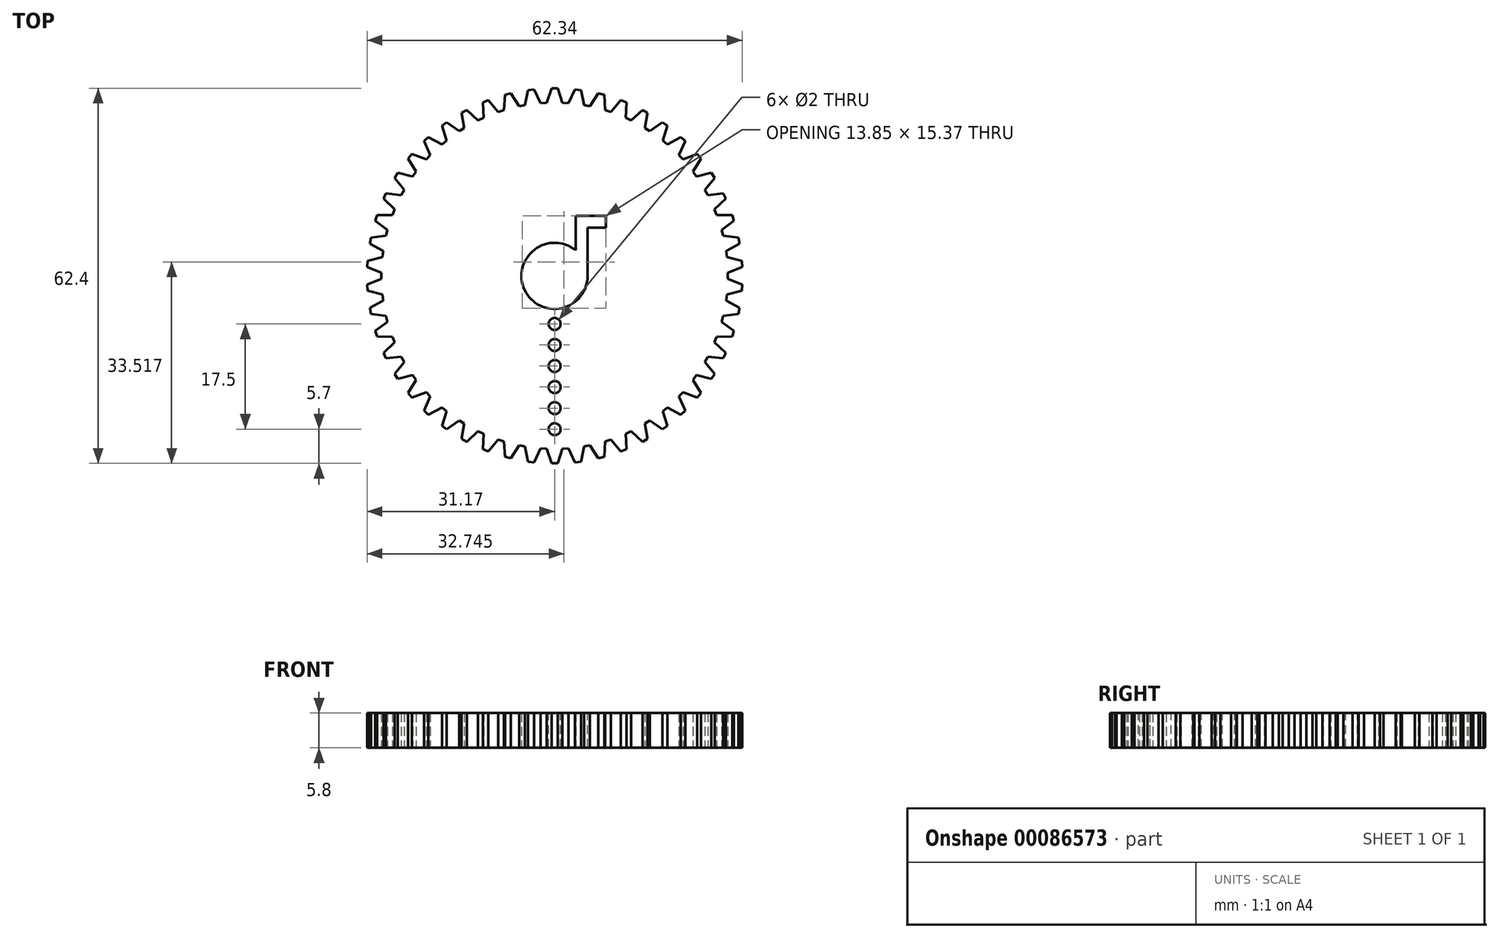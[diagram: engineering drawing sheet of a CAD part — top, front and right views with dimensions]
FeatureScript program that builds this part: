
annotation { "Feature Type Name" : "Feature", "Feature Type Description" : "" }
export const myFeature = defineFeature(function(context is Context, id is Id, definition is map)
    precondition{}
    {
        {
            var Q0;
            Q0=qCreatedBy(makeId("Top.planeOp"),FACE);
            var sketch = newSketch(context, id + "F0", { "sketchPlane" : qUnion([Q0])});
            skCircle(sketch, "E0", {"center": v(0, 0) * mm, "radius": 30 * mm, "construction": true});
            skCircle(sketch, "E1", {"center": v(0, 0) * mm, "radius": 31.2 * mm, "construction": true});
            skCircle(sketch, "E2", {"center": v(0, 0) * mm, "radius": 28.8 * mm, "construction": true});
            skPoint(sketch, "E3", {"position": v(0, 30) * mm});
            skPoint(sketch, "E4.1.0", {"position": v(-3.76, 29.76) * mm});
            skPoint(sketch, "E4.2.0", {"position": v(-7.46, 29.06) * mm});
            skPoint(sketch, "E4.3.0", {"position": v(-11.04, 27.9) * mm});
            skPoint(sketch, "E4.4.0", {"position": v(-14.45, 26.29) * mm});
            skPoint(sketch, "E4.5.0", {"position": v(-17.63, 24.27) * mm});
            skPoint(sketch, "E4.6.0", {"position": v(-20.54, 21.87) * mm});
            skPoint(sketch, "E4.7.0", {"position": v(-23.12, 19.12) * mm});
            skPoint(sketch, "E4.8.0", {"position": v(-25.33, 16.07) * mm});
            skPoint(sketch, "E4.9.0", {"position": v(-27.14, 12.77) * mm});
            skPoint(sketch, "E4.10.0", {"position": v(-28.53, 9.27) * mm});
            skPoint(sketch, "E4.11.0", {"position": v(-29.47, 5.62) * mm});
            skPoint(sketch, "E4.12.0", {"position": v(-29.94, 1.88) * mm});
            skPoint(sketch, "E4.13.0", {"position": v(-29.94, -1.88) * mm});
            skPoint(sketch, "E4.14.0", {"position": v(-29.47, -5.62) * mm});
            skPoint(sketch, "E4.15.0", {"position": v(-28.53, -9.27) * mm});
            skPoint(sketch, "E4.16.0", {"position": v(-27.14, -12.77) * mm});
            skPoint(sketch, "E4.17.0", {"position": v(-25.33, -16.07) * mm});
            skPoint(sketch, "E4.18.0", {"position": v(-23.12, -19.12) * mm});
            skPoint(sketch, "E4.19.0", {"position": v(-20.54, -21.87) * mm});
            skPoint(sketch, "E4.20.0", {"position": v(-17.63, -24.27) * mm});
            skPoint(sketch, "E4.21.0", {"position": v(-14.45, -26.29) * mm});
            skPoint(sketch, "E4.22.0", {"position": v(-11.04, -27.9) * mm});
            skPoint(sketch, "E4.23.0", {"position": v(-7.46, -29.06) * mm});
            skPoint(sketch, "E4.24.0", {"position": v(-3.76, -29.76) * mm});
            skPoint(sketch, "E4.25.0", {"position": v(0, -30) * mm});
            skPoint(sketch, "E4.26.0", {"position": v(3.76, -29.76) * mm});
            skPoint(sketch, "E4.27.0", {"position": v(7.46, -29.06) * mm});
            skPoint(sketch, "E4.28.0", {"position": v(11.04, -27.9) * mm});
            skPoint(sketch, "E4.29.0", {"position": v(14.45, -26.29) * mm});
            skPoint(sketch, "E4.30.0", {"position": v(17.63, -24.27) * mm});
            skPoint(sketch, "E4.31.0", {"position": v(20.54, -21.87) * mm});
            skPoint(sketch, "E4.32.0", {"position": v(23.12, -19.12) * mm});
            skPoint(sketch, "E4.33.0", {"position": v(25.33, -16.07) * mm});
            skPoint(sketch, "E4.34.0", {"position": v(27.14, -12.77) * mm});
            skPoint(sketch, "E4.35.0", {"position": v(28.53, -9.27) * mm});
            skPoint(sketch, "E4.36.0", {"position": v(29.47, -5.62) * mm});
            skPoint(sketch, "E4.37.0", {"position": v(29.94, -1.88) * mm});
            skPoint(sketch, "E4.38.0", {"position": v(29.94, 1.88) * mm});
            skPoint(sketch, "E4.39.0", {"position": v(29.47, 5.62) * mm});
            skPoint(sketch, "E4.40.0", {"position": v(28.53, 9.27) * mm});
            skPoint(sketch, "E4.41.0", {"position": v(27.14, 12.77) * mm});
            skPoint(sketch, "E4.42.0", {"position": v(25.33, 16.07) * mm});
            skPoint(sketch, "E4.43.0", {"position": v(23.12, 19.12) * mm});
            skPoint(sketch, "E4.44.0", {"position": v(20.54, 21.87) * mm});
            skPoint(sketch, "E4.45.0", {"position": v(17.63, 24.27) * mm});
            skPoint(sketch, "E4.46.0", {"position": v(14.45, 26.29) * mm});
            skPoint(sketch, "E4.47.0", {"position": v(11.04, 27.9) * mm});
            skPoint(sketch, "E4.48.0", {"position": v(7.46, 29.06) * mm});
            skPoint(sketch, "E4.49.0", {"position": v(3.76, 29.76) * mm});
            skLineSegment(sketch, "E5", {"start": v(0, 30) * mm, "end": v(3.76, 29.76) * mm, "construction": true});
            skLineSegment(sketch, "E6", {"start": v(1.88, 29.88) * mm, "end": v(0, 0) * mm, "construction": true});
            skLineSegment(sketch, "E7", {"start": v(0, 31.2) * mm, "end": v(0.5, 31.2) * mm});
            skLineSegment(sketch, "E8", {"start": v(1.8, 28.74) * mm, "end": v(1.3, 28.77) * mm});
            skLineSegment(sketch, "E9", {"start": v(0.5, 31.2) * mm, "end": v(1.3, 28.77) * mm});
            skLineSegment(sketch, "E10", {"start": v(3.76, 29.76) * mm, "end": v(0, 0) * mm, "construction": true});
            skLineSegment(sketch, "E11", {"start": v(1.8, 28.74) * mm, "end": v(2.3, 28.71) * mm});
            skLineSegment(sketch, "E12", {"start": v(3.76, 29.76) * mm, "end": v(3.91, 30.95) * mm, "construction": true});
            skLineSegment(sketch, "E13", {"start": v(3.91, 30.95) * mm, "end": v(3.41, 31.02) * mm});
            skLineSegment(sketch, "E14", {"start": v(2.3, 28.71) * mm, "end": v(3.41, 31.02) * mm});
            skLineSegment(sketch, "E15.1.1", {"start": v(-3.76, 29.76) * mm, "end": v(0, 30) * mm, "construction": true});
            skLineSegment(sketch, "E15.1.2", {"start": v(-3.41, 31.02) * mm, "end": v(-2.3, 28.71) * mm});
            skLineSegment(sketch, "E15.1.3", {"start": v(0, 30) * mm, "end": v(0, 31.2) * mm, "construction": true});
            skLineSegment(sketch, "E15.1.4", {"start": v(-1.3, 28.77) * mm, "end": v(-0.5, 31.2) * mm});
            skLineSegment(sketch, "E15.1.6", {"start": v(-3.91, 30.95) * mm, "end": v(-3.41, 31.02) * mm});
            skLineSegment(sketch, "E15.1.7", {"start": v(-1.8, 28.74) * mm, "end": v(-2.3, 28.71) * mm});
            skLineSegment(sketch, "E15.1.8", {"start": v(-1.8, 28.74) * mm, "end": v(-1.3, 28.77) * mm});
            skLineSegment(sketch, "E15.1.9", {"start": v(0, 31.2) * mm, "end": v(-0.5, 31.2) * mm});
            skLineSegment(sketch, "E15.2.1", {"start": v(-7.46, 29.06) * mm, "end": v(-3.76, 29.76) * mm, "construction": true});
            skLineSegment(sketch, "E15.2.2", {"start": v(-7.27, 30.34) * mm, "end": v(-5.89, 28.2) * mm});
            skLineSegment(sketch, "E15.2.3", {"start": v(-3.76, 29.76) * mm, "end": v(-3.91, 30.95) * mm, "construction": true});
            skLineSegment(sketch, "E15.2.4", {"start": v(-4.9, 28.38) * mm, "end": v(-4.4, 30.9) * mm});
            skLineSegment(sketch, "E15.2.6", {"start": v(-7.76, 30.22) * mm, "end": v(-7.27, 30.34) * mm});
            skLineSegment(sketch, "E15.2.7", {"start": v(-5.4, 28.29) * mm, "end": v(-5.89, 28.2) * mm});
            skLineSegment(sketch, "E15.2.8", {"start": v(-5.4, 28.29) * mm, "end": v(-4.9, 28.38) * mm});
            skLineSegment(sketch, "E15.2.9", {"start": v(-3.91, 30.95) * mm, "end": v(-4.4, 30.9) * mm});
            skLineSegment(sketch, "E15.3.1", {"start": v(-11.04, 27.9) * mm, "end": v(-7.46, 29.06) * mm, "construction": true});
            skLineSegment(sketch, "E15.3.2", {"start": v(-11.02, 29.2) * mm, "end": v(-9.38, 27.24) * mm});
            skLineSegment(sketch, "E15.3.3", {"start": v(-7.46, 29.06) * mm, "end": v(-7.76, 30.22) * mm, "construction": true});
            skLineSegment(sketch, "E15.3.4", {"start": v(-8.42, 27.54) * mm, "end": v(-8.24, 30.1) * mm});
            skLineSegment(sketch, "E15.3.6", {"start": v(-11.49, 29) * mm, "end": v(-11.02, 29.2) * mm});
            skLineSegment(sketch, "E15.3.7", {"start": v(-8.9, 27.4) * mm, "end": v(-9.38, 27.24) * mm});
            skLineSegment(sketch, "E15.3.8", {"start": v(-8.9, 27.4) * mm, "end": v(-8.42, 27.54) * mm});
            skLineSegment(sketch, "E15.3.9", {"start": v(-7.76, 30.22) * mm, "end": v(-8.24, 30.1) * mm});
            skLineSegment(sketch, "E15.4.1", {"start": v(-14.45, 26.29) * mm, "end": v(-11.04, 27.9) * mm, "construction": true});
            skLineSegment(sketch, "E15.4.2", {"start": v(-14.6, 27.58) * mm, "end": v(-12.71, 25.85) * mm});
            skLineSegment(sketch, "E15.4.3", {"start": v(-11.04, 27.9) * mm, "end": v(-11.49, 29) * mm, "construction": true});
            skLineSegment(sketch, "E15.4.4", {"start": v(-11.81, 26.27) * mm, "end": v(-11.95, 28.82) * mm});
            skLineSegment(sketch, "E15.4.6", {"start": v(-15.03, 27.34) * mm, "end": v(-14.6, 27.58) * mm});
            skLineSegment(sketch, "E15.4.7", {"start": v(-12.26, 26.06) * mm, "end": v(-12.71, 25.85) * mm});
            skLineSegment(sketch, "E15.4.8", {"start": v(-12.26, 26.06) * mm, "end": v(-11.81, 26.27) * mm});
            skLineSegment(sketch, "E15.4.9", {"start": v(-11.49, 29) * mm, "end": v(-11.95, 28.82) * mm});
            skLineSegment(sketch, "E15.5.1", {"start": v(-17.63, 24.27) * mm, "end": v(-14.45, 26.29) * mm, "construction": true});
            skLineSegment(sketch, "E15.5.2", {"start": v(-17.93, 25.54) * mm, "end": v(-15.85, 24.05) * mm});
            skLineSegment(sketch, "E15.5.3", {"start": v(-14.45, 26.29) * mm, "end": v(-15.03, 27.34) * mm, "construction": true});
            skLineSegment(sketch, "E15.5.4", {"start": v(-15, 24.58) * mm, "end": v(-15.47, 27.1) * mm});
            skLineSegment(sketch, "E15.5.6", {"start": v(-18.34, 25.24) * mm, "end": v(-17.93, 25.54) * mm});
            skLineSegment(sketch, "E15.5.7", {"start": v(-15.43, 24.32) * mm, "end": v(-15.85, 24.05) * mm});
            skLineSegment(sketch, "E15.5.8", {"start": v(-15.43, 24.32) * mm, "end": v(-15, 24.58) * mm});
            skLineSegment(sketch, "E15.5.9", {"start": v(-15.03, 27.34) * mm, "end": v(-15.47, 27.1) * mm});
            skLineSegment(sketch, "E15.6.1", {"start": v(-20.54, 21.87) * mm, "end": v(-17.63, 24.27) * mm, "construction": true});
            skLineSegment(sketch, "E15.6.2", {"start": v(-21, 23.09) * mm, "end": v(-18.74, 21.87) * mm});
            skLineSegment(sketch, "E15.6.3", {"start": v(-17.63, 24.27) * mm, "end": v(-18.34, 25.24) * mm, "construction": true});
            skLineSegment(sketch, "E15.6.4", {"start": v(-17.97, 22.5) * mm, "end": v(-18.74, 24.95) * mm});
            skLineSegment(sketch, "E15.6.6", {"start": v(-21.36, 22.74) * mm, "end": v(-21, 23.09) * mm});
            skLineSegment(sketch, "E15.6.7", {"start": v(-18.36, 22.2) * mm, "end": v(-18.74, 21.87) * mm});
            skLineSegment(sketch, "E15.6.8", {"start": v(-18.36, 22.2) * mm, "end": v(-17.97, 22.5) * mm});
            skLineSegment(sketch, "E15.6.9", {"start": v(-18.34, 25.24) * mm, "end": v(-18.74, 24.95) * mm});
            skLineSegment(sketch, "E15.7.1", {"start": v(-23.12, 19.12) * mm, "end": v(-20.54, 21.87) * mm, "construction": true});
            skLineSegment(sketch, "E15.7.2", {"start": v(-23.72, 20.27) * mm, "end": v(-21.34, 19.35) * mm});
            skLineSegment(sketch, "E15.7.3", {"start": v(-20.54, 21.87) * mm, "end": v(-21.36, 22.74) * mm, "construction": true});
            skLineSegment(sketch, "E15.7.4", {"start": v(-20.65, 20.08) * mm, "end": v(-21.72, 22.4) * mm});
            skLineSegment(sketch, "E15.7.6", {"start": v(-24.04, 19.89) * mm, "end": v(-23.72, 20.27) * mm});
            skLineSegment(sketch, "E15.7.7", {"start": v(-21, 19.71) * mm, "end": v(-21.34, 19.35) * mm});
            skLineSegment(sketch, "E15.7.8", {"start": v(-21, 19.71) * mm, "end": v(-20.65, 20.08) * mm});
            skLineSegment(sketch, "E15.7.9", {"start": v(-21.36, 22.74) * mm, "end": v(-21.72, 22.4) * mm});
            skLineSegment(sketch, "E15.8.1", {"start": v(-25.33, 16.07) * mm, "end": v(-23.12, 19.12) * mm, "construction": true});
            skLineSegment(sketch, "E15.8.2", {"start": v(-26.08, 17.14) * mm, "end": v(-23.6, 16.52) * mm});
            skLineSegment(sketch, "E15.8.3", {"start": v(-23.12, 19.12) * mm, "end": v(-24.04, 19.89) * mm, "construction": true});
            skLineSegment(sketch, "E15.8.4", {"start": v(-23, 17.33) * mm, "end": v(-24.36, 19.5) * mm});
            skLineSegment(sketch, "E15.8.6", {"start": v(-26.34, 16.72) * mm, "end": v(-26.08, 17.14) * mm});
            skLineSegment(sketch, "E15.8.7", {"start": v(-23.3, 16.93) * mm, "end": v(-23.6, 16.52) * mm});
            skLineSegment(sketch, "E15.8.8", {"start": v(-23.3, 16.93) * mm, "end": v(-23, 17.33) * mm});
            skLineSegment(sketch, "E15.8.9", {"start": v(-24.04, 19.89) * mm, "end": v(-24.36, 19.5) * mm});
            skLineSegment(sketch, "E15.9.1", {"start": v(-27.14, 12.77) * mm, "end": v(-25.33, 16.07) * mm, "construction": true});
            skLineSegment(sketch, "E15.9.2", {"start": v(-28.02, 13.74) * mm, "end": v(-25.48, 13.44) * mm});
            skLineSegment(sketch, "E15.9.3", {"start": v(-25.33, 16.07) * mm, "end": v(-26.34, 16.72) * mm, "construction": true});
            skLineSegment(sketch, "E15.9.4", {"start": v(-25, 14.31) * mm, "end": v(-26.61, 16.3) * mm});
            skLineSegment(sketch, "E15.9.6", {"start": v(-28.23, 13.28) * mm, "end": v(-28.02, 13.74) * mm});
            skLineSegment(sketch, "E15.9.7", {"start": v(-25.24, 13.87) * mm, "end": v(-25.48, 13.44) * mm});
            skLineSegment(sketch, "E15.9.8", {"start": v(-25.24, 13.87) * mm, "end": v(-25, 14.31) * mm});
            skLineSegment(sketch, "E15.9.9", {"start": v(-26.34, 16.72) * mm, "end": v(-26.61, 16.3) * mm});
            skLineSegment(sketch, "E15.10.1", {"start": v(-28.53, 9.27) * mm, "end": v(-27.14, 12.77) * mm, "construction": true});
            skLineSegment(sketch, "E15.10.2", {"start": v(-29.52, 10.12) * mm, "end": v(-26.96, 10.14) * mm});
            skLineSegment(sketch, "E15.10.3", {"start": v(-27.14, 12.77) * mm, "end": v(-28.23, 13.28) * mm, "construction": true});
            skLineSegment(sketch, "E15.10.4", {"start": v(-26.6, 11.07) * mm, "end": v(-28.44, 12.83) * mm});
            skLineSegment(sketch, "E15.10.6", {"start": v(-29.67, 9.64) * mm, "end": v(-29.52, 10.12) * mm});
            skLineSegment(sketch, "E15.10.7", {"start": v(-26.78, 10.6) * mm, "end": v(-26.96, 10.14) * mm});
            skLineSegment(sketch, "E15.10.8", {"start": v(-26.78, 10.6) * mm, "end": v(-26.6, 11.07) * mm});
            skLineSegment(sketch, "E15.10.9", {"start": v(-28.23, 13.28) * mm, "end": v(-28.44, 12.83) * mm});
            skLineSegment(sketch, "E15.11.1", {"start": v(-29.47, 5.62) * mm, "end": v(-28.53, 9.27) * mm, "construction": true});
            skLineSegment(sketch, "E15.11.2", {"start": v(-30.55, 6.34) * mm, "end": v(-28.02, 6.68) * mm});
            skLineSegment(sketch, "E15.11.3", {"start": v(-28.53, 9.27) * mm, "end": v(-29.67, 9.64) * mm, "construction": true});
            skLineSegment(sketch, "E15.11.4", {"start": v(-27.77, 7.65) * mm, "end": v(-29.83, 9.17) * mm});
            skLineSegment(sketch, "E15.11.6", {"start": v(-30.65, 5.85) * mm, "end": v(-30.55, 6.34) * mm});
            skLineSegment(sketch, "E15.11.7", {"start": v(-27.9, 7.16) * mm, "end": v(-28.02, 6.68) * mm});
            skLineSegment(sketch, "E15.11.8", {"start": v(-27.9, 7.16) * mm, "end": v(-27.77, 7.65) * mm});
            skLineSegment(sketch, "E15.11.9", {"start": v(-29.67, 9.64) * mm, "end": v(-29.83, 9.17) * mm});
            skLineSegment(sketch, "E15.12.1", {"start": v(-29.94, 1.88) * mm, "end": v(-29.47, 5.62) * mm, "construction": true});
            skLineSegment(sketch, "E15.12.2", {"start": v(-31.1, 2.46) * mm, "end": v(-28.64, 3.11) * mm});
            skLineSegment(sketch, "E15.12.3", {"start": v(-29.47, 5.62) * mm, "end": v(-30.65, 5.85) * mm, "construction": true});
            skLineSegment(sketch, "E15.12.4", {"start": v(-28.51, 4.1) * mm, "end": v(-30.74, 5.36) * mm});
            skLineSegment(sketch, "E15.12.6", {"start": v(-31.14, 1.96) * mm, "end": v(-31.1, 2.46) * mm});
            skLineSegment(sketch, "E15.12.7", {"start": v(-28.57, 3.6) * mm, "end": v(-28.64, 3.11) * mm});
            skLineSegment(sketch, "E15.12.8", {"start": v(-28.57, 3.6) * mm, "end": v(-28.51, 4.1) * mm});
            skLineSegment(sketch, "E15.12.9", {"start": v(-30.65, 5.85) * mm, "end": v(-30.74, 5.36) * mm});
            skLineSegment(sketch, "E15.13.1", {"start": v(-29.94, -1.88) * mm, "end": v(-29.94, 1.88) * mm, "construction": true});
            skLineSegment(sketch, "E15.13.2", {"start": v(-31.17, -1.46) * mm, "end": v(-28.8, -0.5) * mm});
            skLineSegment(sketch, "E15.13.3", {"start": v(-29.94, 1.88) * mm, "end": v(-31.14, 1.96) * mm, "construction": true});
            skLineSegment(sketch, "E15.13.4", {"start": v(-28.8, 0.5) * mm, "end": v(-31.17, 1.46) * mm});
            skLineSegment(sketch, "E15.13.6", {"start": v(-31.14, -1.96) * mm, "end": v(-31.17, -1.46) * mm});
            skLineSegment(sketch, "E15.13.7", {"start": v(-28.8, 0) * mm, "end": v(-28.8, -0.5) * mm});
            skLineSegment(sketch, "E15.13.8", {"start": v(-28.8, 0) * mm, "end": v(-28.8, 0.5) * mm});
            skLineSegment(sketch, "E15.13.9", {"start": v(-31.14, 1.96) * mm, "end": v(-31.17, 1.46) * mm});
            skLineSegment(sketch, "E15.14.1", {"start": v(-29.47, -5.62) * mm, "end": v(-29.94, -1.88) * mm, "construction": true});
            skLineSegment(sketch, "E15.14.2", {"start": v(-30.74, -5.36) * mm, "end": v(-28.51, -4.1) * mm});
            skLineSegment(sketch, "E15.14.3", {"start": v(-29.94, -1.88) * mm, "end": v(-31.14, -1.96) * mm, "construction": true});
            skLineSegment(sketch, "E15.14.4", {"start": v(-28.64, -3.11) * mm, "end": v(-31.1, -2.46) * mm});
            skLineSegment(sketch, "E15.14.6", {"start": v(-30.65, -5.85) * mm, "end": v(-30.74, -5.36) * mm});
            skLineSegment(sketch, "E15.14.7", {"start": v(-28.57, -3.6) * mm, "end": v(-28.51, -4.1) * mm});
            skLineSegment(sketch, "E15.14.8", {"start": v(-28.57, -3.6) * mm, "end": v(-28.64, -3.11) * mm});
            skLineSegment(sketch, "E15.14.9", {"start": v(-31.14, -1.96) * mm, "end": v(-31.1, -2.46) * mm});
            skLineSegment(sketch, "E15.15.1", {"start": v(-28.53, -9.27) * mm, "end": v(-29.47, -5.62) * mm, "construction": true});
            skLineSegment(sketch, "E15.15.2", {"start": v(-29.83, -9.17) * mm, "end": v(-27.77, -7.65) * mm});
            skLineSegment(sketch, "E15.15.3", {"start": v(-29.47, -5.62) * mm, "end": v(-30.65, -5.85) * mm, "construction": true});
            skLineSegment(sketch, "E15.15.4", {"start": v(-28.02, -6.68) * mm, "end": v(-30.55, -6.34) * mm});
            skLineSegment(sketch, "E15.15.6", {"start": v(-29.67, -9.64) * mm, "end": v(-29.83, -9.17) * mm});
            skLineSegment(sketch, "E15.15.7", {"start": v(-27.9, -7.16) * mm, "end": v(-27.77, -7.65) * mm});
            skLineSegment(sketch, "E15.15.8", {"start": v(-27.9, -7.16) * mm, "end": v(-28.02, -6.68) * mm});
            skLineSegment(sketch, "E15.15.9", {"start": v(-30.65, -5.85) * mm, "end": v(-30.55, -6.34) * mm});
            skLineSegment(sketch, "E15.16.1", {"start": v(-27.14, -12.77) * mm, "end": v(-28.53, -9.27) * mm, "construction": true});
            skLineSegment(sketch, "E15.16.2", {"start": v(-28.44, -12.83) * mm, "end": v(-26.6, -11.07) * mm});
            skLineSegment(sketch, "E15.16.3", {"start": v(-28.53, -9.27) * mm, "end": v(-29.67, -9.64) * mm, "construction": true});
            skLineSegment(sketch, "E15.16.4", {"start": v(-26.96, -10.14) * mm, "end": v(-29.52, -10.12) * mm});
            skLineSegment(sketch, "E15.16.6", {"start": v(-28.23, -13.28) * mm, "end": v(-28.44, -12.83) * mm});
            skLineSegment(sketch, "E15.16.7", {"start": v(-26.78, -10.6) * mm, "end": v(-26.6, -11.07) * mm});
            skLineSegment(sketch, "E15.16.8", {"start": v(-26.78, -10.6) * mm, "end": v(-26.96, -10.14) * mm});
            skLineSegment(sketch, "E15.16.9", {"start": v(-29.67, -9.64) * mm, "end": v(-29.52, -10.12) * mm});
            skLineSegment(sketch, "E15.17.1", {"start": v(-25.33, -16.07) * mm, "end": v(-27.14, -12.77) * mm, "construction": true});
            skLineSegment(sketch, "E15.17.2", {"start": v(-26.61, -16.3) * mm, "end": v(-25, -14.31) * mm});
            skLineSegment(sketch, "E15.17.3", {"start": v(-27.14, -12.77) * mm, "end": v(-28.23, -13.28) * mm, "construction": true});
            skLineSegment(sketch, "E15.17.4", {"start": v(-25.48, -13.44) * mm, "end": v(-28.02, -13.74) * mm});
            skLineSegment(sketch, "E15.17.6", {"start": v(-26.34, -16.72) * mm, "end": v(-26.61, -16.3) * mm});
            skLineSegment(sketch, "E15.17.7", {"start": v(-25.24, -13.87) * mm, "end": v(-25, -14.31) * mm});
            skLineSegment(sketch, "E15.17.8", {"start": v(-25.24, -13.87) * mm, "end": v(-25.48, -13.44) * mm});
            skLineSegment(sketch, "E15.17.9", {"start": v(-28.23, -13.28) * mm, "end": v(-28.02, -13.74) * mm});
            skLineSegment(sketch, "E15.18.1", {"start": v(-23.12, -19.12) * mm, "end": v(-25.33, -16.07) * mm, "construction": true});
            skLineSegment(sketch, "E15.18.2", {"start": v(-24.36, -19.5) * mm, "end": v(-23, -17.33) * mm});
            skLineSegment(sketch, "E15.18.3", {"start": v(-25.33, -16.07) * mm, "end": v(-26.34, -16.72) * mm, "construction": true});
            skLineSegment(sketch, "E15.18.4", {"start": v(-23.6, -16.52) * mm, "end": v(-26.08, -17.14) * mm});
            skLineSegment(sketch, "E15.18.6", {"start": v(-24.04, -19.89) * mm, "end": v(-24.36, -19.5) * mm});
            skLineSegment(sketch, "E15.18.7", {"start": v(-23.3, -16.93) * mm, "end": v(-23, -17.33) * mm});
            skLineSegment(sketch, "E15.18.8", {"start": v(-23.3, -16.93) * mm, "end": v(-23.6, -16.52) * mm});
            skLineSegment(sketch, "E15.18.9", {"start": v(-26.34, -16.72) * mm, "end": v(-26.08, -17.14) * mm});
            skLineSegment(sketch, "E15.19.1", {"start": v(-20.54, -21.87) * mm, "end": v(-23.12, -19.12) * mm, "construction": true});
            skLineSegment(sketch, "E15.19.2", {"start": v(-21.72, -22.4) * mm, "end": v(-20.65, -20.08) * mm});
            skLineSegment(sketch, "E15.19.3", {"start": v(-23.12, -19.12) * mm, "end": v(-24.04, -19.89) * mm, "construction": true});
            skLineSegment(sketch, "E15.19.4", {"start": v(-21.34, -19.35) * mm, "end": v(-23.72, -20.27) * mm});
            skLineSegment(sketch, "E15.19.6", {"start": v(-21.36, -22.74) * mm, "end": v(-21.72, -22.4) * mm});
            skLineSegment(sketch, "E15.19.7", {"start": v(-21, -19.71) * mm, "end": v(-20.65, -20.08) * mm});
            skLineSegment(sketch, "E15.19.8", {"start": v(-21, -19.71) * mm, "end": v(-21.34, -19.35) * mm});
            skLineSegment(sketch, "E15.19.9", {"start": v(-24.04, -19.89) * mm, "end": v(-23.72, -20.27) * mm});
            skLineSegment(sketch, "E15.20.1", {"start": v(-17.63, -24.27) * mm, "end": v(-20.54, -21.87) * mm, "construction": true});
            skLineSegment(sketch, "E15.20.2", {"start": v(-18.74, -24.95) * mm, "end": v(-17.97, -22.5) * mm});
            skLineSegment(sketch, "E15.20.3", {"start": v(-20.54, -21.87) * mm, "end": v(-21.36, -22.74) * mm, "construction": true});
            skLineSegment(sketch, "E15.20.4", {"start": v(-18.74, -21.87) * mm, "end": v(-21, -23.09) * mm});
            skLineSegment(sketch, "E15.20.6", {"start": v(-18.34, -25.24) * mm, "end": v(-18.74, -24.95) * mm});
            skLineSegment(sketch, "E15.20.7", {"start": v(-18.36, -22.2) * mm, "end": v(-17.97, -22.5) * mm});
            skLineSegment(sketch, "E15.20.8", {"start": v(-18.36, -22.2) * mm, "end": v(-18.74, -21.87) * mm});
            skLineSegment(sketch, "E15.20.9", {"start": v(-21.36, -22.74) * mm, "end": v(-21, -23.09) * mm});
            skLineSegment(sketch, "E15.21.1", {"start": v(-14.45, -26.29) * mm, "end": v(-17.63, -24.27) * mm, "construction": true});
            skLineSegment(sketch, "E15.21.2", {"start": v(-15.47, -27.1) * mm, "end": v(-15, -24.58) * mm});
            skLineSegment(sketch, "E15.21.3", {"start": v(-17.63, -24.27) * mm, "end": v(-18.34, -25.24) * mm, "construction": true});
            skLineSegment(sketch, "E15.21.4", {"start": v(-15.85, -24.05) * mm, "end": v(-17.93, -25.54) * mm});
            skLineSegment(sketch, "E15.21.6", {"start": v(-15.03, -27.34) * mm, "end": v(-15.47, -27.1) * mm});
            skLineSegment(sketch, "E15.21.7", {"start": v(-15.43, -24.32) * mm, "end": v(-15, -24.58) * mm});
            skLineSegment(sketch, "E15.21.8", {"start": v(-15.43, -24.32) * mm, "end": v(-15.85, -24.05) * mm});
            skLineSegment(sketch, "E15.21.9", {"start": v(-18.34, -25.24) * mm, "end": v(-17.93, -25.54) * mm});
            skLineSegment(sketch, "E15.22.1", {"start": v(-11.04, -27.9) * mm, "end": v(-14.45, -26.29) * mm, "construction": true});
            skLineSegment(sketch, "E15.22.2", {"start": v(-11.95, -28.82) * mm, "end": v(-11.81, -26.27) * mm});
            skLineSegment(sketch, "E15.22.3", {"start": v(-14.45, -26.29) * mm, "end": v(-15.03, -27.34) * mm, "construction": true});
            skLineSegment(sketch, "E15.22.4", {"start": v(-12.71, -25.85) * mm, "end": v(-14.6, -27.58) * mm});
            skLineSegment(sketch, "E15.22.6", {"start": v(-11.49, -29) * mm, "end": v(-11.95, -28.82) * mm});
            skLineSegment(sketch, "E15.22.7", {"start": v(-12.26, -26.06) * mm, "end": v(-11.81, -26.27) * mm});
            skLineSegment(sketch, "E15.22.8", {"start": v(-12.26, -26.06) * mm, "end": v(-12.71, -25.85) * mm});
            skLineSegment(sketch, "E15.22.9", {"start": v(-15.03, -27.34) * mm, "end": v(-14.6, -27.58) * mm});
            skLineSegment(sketch, "E15.23.1", {"start": v(-7.46, -29.06) * mm, "end": v(-11.04, -27.9) * mm, "construction": true});
            skLineSegment(sketch, "E15.23.2", {"start": v(-8.24, -30.1) * mm, "end": v(-8.42, -27.54) * mm});
            skLineSegment(sketch, "E15.23.3", {"start": v(-11.04, -27.9) * mm, "end": v(-11.49, -29) * mm, "construction": true});
            skLineSegment(sketch, "E15.23.4", {"start": v(-9.38, -27.24) * mm, "end": v(-11.02, -29.2) * mm});
            skLineSegment(sketch, "E15.23.6", {"start": v(-7.76, -30.22) * mm, "end": v(-8.24, -30.1) * mm});
            skLineSegment(sketch, "E15.23.7", {"start": v(-8.9, -27.4) * mm, "end": v(-8.42, -27.54) * mm});
            skLineSegment(sketch, "E15.23.8", {"start": v(-8.9, -27.4) * mm, "end": v(-9.38, -27.24) * mm});
            skLineSegment(sketch, "E15.23.9", {"start": v(-11.49, -29) * mm, "end": v(-11.02, -29.2) * mm});
            skLineSegment(sketch, "E15.24.1", {"start": v(-3.76, -29.76) * mm, "end": v(-7.46, -29.06) * mm, "construction": true});
            skLineSegment(sketch, "E15.24.2", {"start": v(-4.4, -30.9) * mm, "end": v(-4.9, -28.38) * mm});
            skLineSegment(sketch, "E15.24.3", {"start": v(-7.46, -29.06) * mm, "end": v(-7.76, -30.22) * mm, "construction": true});
            skLineSegment(sketch, "E15.24.4", {"start": v(-5.89, -28.2) * mm, "end": v(-7.27, -30.34) * mm});
            skLineSegment(sketch, "E15.24.6", {"start": v(-3.91, -30.95) * mm, "end": v(-4.4, -30.9) * mm});
            skLineSegment(sketch, "E15.24.7", {"start": v(-5.4, -28.29) * mm, "end": v(-4.9, -28.38) * mm});
            skLineSegment(sketch, "E15.24.8", {"start": v(-5.4, -28.29) * mm, "end": v(-5.89, -28.2) * mm});
            skLineSegment(sketch, "E15.24.9", {"start": v(-7.76, -30.22) * mm, "end": v(-7.27, -30.34) * mm});
            skLineSegment(sketch, "E15.25.1", {"start": v(0, -30) * mm, "end": v(-3.76, -29.76) * mm, "construction": true});
            skLineSegment(sketch, "E15.25.2", {"start": v(-0.5, -31.2) * mm, "end": v(-1.3, -28.77) * mm});
            skLineSegment(sketch, "E15.25.3", {"start": v(-3.76, -29.76) * mm, "end": v(-3.91, -30.95) * mm, "construction": true});
            skLineSegment(sketch, "E15.25.4", {"start": v(-2.3, -28.71) * mm, "end": v(-3.41, -31.02) * mm});
            skLineSegment(sketch, "E15.25.6", {"start": v(0, -31.2) * mm, "end": v(-0.5, -31.2) * mm});
            skLineSegment(sketch, "E15.25.7", {"start": v(-1.8, -28.74) * mm, "end": v(-1.3, -28.77) * mm});
            skLineSegment(sketch, "E15.25.8", {"start": v(-1.8, -28.74) * mm, "end": v(-2.3, -28.71) * mm});
            skLineSegment(sketch, "E15.25.9", {"start": v(-3.91, -30.95) * mm, "end": v(-3.41, -31.02) * mm});
            skLineSegment(sketch, "E15.26.1", {"start": v(3.76, -29.76) * mm, "end": v(0, -30) * mm, "construction": true});
            skLineSegment(sketch, "E15.26.2", {"start": v(3.41, -31.02) * mm, "end": v(2.3, -28.71) * mm});
            skLineSegment(sketch, "E15.26.3", {"start": v(0, -30) * mm, "end": v(0, -31.2) * mm, "construction": true});
            skLineSegment(sketch, "E15.26.4", {"start": v(1.3, -28.77) * mm, "end": v(0.5, -31.2) * mm});
            skLineSegment(sketch, "E15.26.6", {"start": v(3.91, -30.95) * mm, "end": v(3.41, -31.02) * mm});
            skLineSegment(sketch, "E15.26.7", {"start": v(1.8, -28.74) * mm, "end": v(2.3, -28.71) * mm});
            skLineSegment(sketch, "E15.26.8", {"start": v(1.8, -28.74) * mm, "end": v(1.3, -28.77) * mm});
            skLineSegment(sketch, "E15.26.9", {"start": v(0, -31.2) * mm, "end": v(0.5, -31.2) * mm});
            skLineSegment(sketch, "E15.27.1", {"start": v(7.46, -29.06) * mm, "end": v(3.76, -29.76) * mm, "construction": true});
            skLineSegment(sketch, "E15.27.2", {"start": v(7.27, -30.34) * mm, "end": v(5.89, -28.2) * mm});
            skLineSegment(sketch, "E15.27.3", {"start": v(3.76, -29.76) * mm, "end": v(3.91, -30.95) * mm, "construction": true});
            skLineSegment(sketch, "E15.27.4", {"start": v(4.9, -28.38) * mm, "end": v(4.4, -30.9) * mm});
            skLineSegment(sketch, "E15.27.6", {"start": v(7.76, -30.22) * mm, "end": v(7.27, -30.34) * mm});
            skLineSegment(sketch, "E15.27.7", {"start": v(5.4, -28.29) * mm, "end": v(5.89, -28.2) * mm});
            skLineSegment(sketch, "E15.27.8", {"start": v(5.4, -28.29) * mm, "end": v(4.9, -28.38) * mm});
            skLineSegment(sketch, "E15.27.9", {"start": v(3.91, -30.95) * mm, "end": v(4.4, -30.9) * mm});
            skLineSegment(sketch, "E15.28.1", {"start": v(11.04, -27.9) * mm, "end": v(7.46, -29.06) * mm, "construction": true});
            skLineSegment(sketch, "E15.28.2", {"start": v(11.02, -29.2) * mm, "end": v(9.38, -27.24) * mm});
            skLineSegment(sketch, "E15.28.3", {"start": v(7.46, -29.06) * mm, "end": v(7.76, -30.22) * mm, "construction": true});
            skLineSegment(sketch, "E15.28.4", {"start": v(8.42, -27.54) * mm, "end": v(8.24, -30.1) * mm});
            skLineSegment(sketch, "E15.28.6", {"start": v(11.49, -29) * mm, "end": v(11.02, -29.2) * mm});
            skLineSegment(sketch, "E15.28.7", {"start": v(8.9, -27.4) * mm, "end": v(9.38, -27.24) * mm});
            skLineSegment(sketch, "E15.28.8", {"start": v(8.9, -27.4) * mm, "end": v(8.42, -27.54) * mm});
            skLineSegment(sketch, "E15.28.9", {"start": v(7.76, -30.22) * mm, "end": v(8.24, -30.1) * mm});
            skLineSegment(sketch, "E15.29.1", {"start": v(14.45, -26.29) * mm, "end": v(11.04, -27.9) * mm, "construction": true});
            skLineSegment(sketch, "E15.29.2", {"start": v(14.6, -27.58) * mm, "end": v(12.71, -25.85) * mm});
            skLineSegment(sketch, "E15.29.3", {"start": v(11.04, -27.9) * mm, "end": v(11.49, -29) * mm, "construction": true});
            skLineSegment(sketch, "E15.29.4", {"start": v(11.81, -26.27) * mm, "end": v(11.95, -28.82) * mm});
            skLineSegment(sketch, "E15.29.6", {"start": v(15.03, -27.34) * mm, "end": v(14.6, -27.58) * mm});
            skLineSegment(sketch, "E15.29.7", {"start": v(12.26, -26.06) * mm, "end": v(12.71, -25.85) * mm});
            skLineSegment(sketch, "E15.29.8", {"start": v(12.26, -26.06) * mm, "end": v(11.81, -26.27) * mm});
            skLineSegment(sketch, "E15.29.9", {"start": v(11.49, -29) * mm, "end": v(11.95, -28.82) * mm});
            skLineSegment(sketch, "E15.30.1", {"start": v(17.63, -24.27) * mm, "end": v(14.45, -26.29) * mm, "construction": true});
            skLineSegment(sketch, "E15.30.2", {"start": v(17.93, -25.54) * mm, "end": v(15.85, -24.05) * mm});
            skLineSegment(sketch, "E15.30.3", {"start": v(14.45, -26.29) * mm, "end": v(15.03, -27.34) * mm, "construction": true});
            skLineSegment(sketch, "E15.30.4", {"start": v(15, -24.58) * mm, "end": v(15.47, -27.1) * mm});
            skLineSegment(sketch, "E15.30.6", {"start": v(18.34, -25.24) * mm, "end": v(17.93, -25.54) * mm});
            skLineSegment(sketch, "E15.30.7", {"start": v(15.43, -24.32) * mm, "end": v(15.85, -24.05) * mm});
            skLineSegment(sketch, "E15.30.8", {"start": v(15.43, -24.32) * mm, "end": v(15, -24.58) * mm});
            skLineSegment(sketch, "E15.30.9", {"start": v(15.03, -27.34) * mm, "end": v(15.47, -27.1) * mm});
            skLineSegment(sketch, "E15.31.1", {"start": v(20.54, -21.87) * mm, "end": v(17.63, -24.27) * mm, "construction": true});
            skLineSegment(sketch, "E15.31.2", {"start": v(21, -23.09) * mm, "end": v(18.74, -21.87) * mm});
            skLineSegment(sketch, "E15.31.3", {"start": v(17.63, -24.27) * mm, "end": v(18.34, -25.24) * mm, "construction": true});
            skLineSegment(sketch, "E15.31.4", {"start": v(17.97, -22.5) * mm, "end": v(18.74, -24.95) * mm});
            skLineSegment(sketch, "E15.31.6", {"start": v(21.36, -22.74) * mm, "end": v(21, -23.09) * mm});
            skLineSegment(sketch, "E15.31.7", {"start": v(18.36, -22.2) * mm, "end": v(18.74, -21.87) * mm});
            skLineSegment(sketch, "E15.31.8", {"start": v(18.36, -22.2) * mm, "end": v(17.97, -22.5) * mm});
            skLineSegment(sketch, "E15.31.9", {"start": v(18.34, -25.24) * mm, "end": v(18.74, -24.95) * mm});
            skLineSegment(sketch, "E15.32.1", {"start": v(23.12, -19.12) * mm, "end": v(20.54, -21.87) * mm, "construction": true});
            skLineSegment(sketch, "E15.32.2", {"start": v(23.72, -20.27) * mm, "end": v(21.34, -19.35) * mm});
            skLineSegment(sketch, "E15.32.3", {"start": v(20.54, -21.87) * mm, "end": v(21.36, -22.74) * mm, "construction": true});
            skLineSegment(sketch, "E15.32.4", {"start": v(20.65, -20.08) * mm, "end": v(21.72, -22.4) * mm});
            skLineSegment(sketch, "E15.32.6", {"start": v(24.04, -19.89) * mm, "end": v(23.72, -20.27) * mm});
            skLineSegment(sketch, "E15.32.7", {"start": v(21, -19.71) * mm, "end": v(21.34, -19.35) * mm});
            skLineSegment(sketch, "E15.32.8", {"start": v(21, -19.71) * mm, "end": v(20.65, -20.08) * mm});
            skLineSegment(sketch, "E15.32.9", {"start": v(21.36, -22.74) * mm, "end": v(21.72, -22.4) * mm});
            skLineSegment(sketch, "E15.33.1", {"start": v(25.33, -16.07) * mm, "end": v(23.12, -19.12) * mm, "construction": true});
            skLineSegment(sketch, "E15.33.2", {"start": v(26.08, -17.14) * mm, "end": v(23.6, -16.52) * mm});
            skLineSegment(sketch, "E15.33.3", {"start": v(23.12, -19.12) * mm, "end": v(24.04, -19.89) * mm, "construction": true});
            skLineSegment(sketch, "E15.33.4", {"start": v(23, -17.33) * mm, "end": v(24.36, -19.5) * mm});
            skLineSegment(sketch, "E15.33.6", {"start": v(26.34, -16.72) * mm, "end": v(26.08, -17.14) * mm});
            skLineSegment(sketch, "E15.33.7", {"start": v(23.3, -16.93) * mm, "end": v(23.6, -16.52) * mm});
            skLineSegment(sketch, "E15.33.8", {"start": v(23.3, -16.93) * mm, "end": v(23, -17.33) * mm});
            skLineSegment(sketch, "E15.33.9", {"start": v(24.04, -19.89) * mm, "end": v(24.36, -19.5) * mm});
            skLineSegment(sketch, "E15.34.1", {"start": v(27.14, -12.77) * mm, "end": v(25.33, -16.07) * mm, "construction": true});
            skLineSegment(sketch, "E15.34.2", {"start": v(28.02, -13.74) * mm, "end": v(25.48, -13.44) * mm});
            skLineSegment(sketch, "E15.34.3", {"start": v(25.33, -16.07) * mm, "end": v(26.34, -16.72) * mm, "construction": true});
            skLineSegment(sketch, "E15.34.4", {"start": v(25, -14.31) * mm, "end": v(26.61, -16.3) * mm});
            skLineSegment(sketch, "E15.34.6", {"start": v(28.23, -13.28) * mm, "end": v(28.02, -13.74) * mm});
            skLineSegment(sketch, "E15.34.7", {"start": v(25.24, -13.87) * mm, "end": v(25.48, -13.44) * mm});
            skLineSegment(sketch, "E15.34.8", {"start": v(25.24, -13.87) * mm, "end": v(25, -14.31) * mm});
            skLineSegment(sketch, "E15.34.9", {"start": v(26.34, -16.72) * mm, "end": v(26.61, -16.3) * mm});
            skLineSegment(sketch, "E15.35.1", {"start": v(28.53, -9.27) * mm, "end": v(27.14, -12.77) * mm, "construction": true});
            skLineSegment(sketch, "E15.35.2", {"start": v(29.52, -10.12) * mm, "end": v(26.96, -10.14) * mm});
            skLineSegment(sketch, "E15.35.3", {"start": v(27.14, -12.77) * mm, "end": v(28.23, -13.28) * mm, "construction": true});
            skLineSegment(sketch, "E15.35.4", {"start": v(26.6, -11.07) * mm, "end": v(28.44, -12.83) * mm});
            skLineSegment(sketch, "E15.35.6", {"start": v(29.67, -9.64) * mm, "end": v(29.52, -10.12) * mm});
            skLineSegment(sketch, "E15.35.7", {"start": v(26.78, -10.6) * mm, "end": v(26.96, -10.14) * mm});
            skLineSegment(sketch, "E15.35.8", {"start": v(26.78, -10.6) * mm, "end": v(26.6, -11.07) * mm});
            skLineSegment(sketch, "E15.35.9", {"start": v(28.23, -13.28) * mm, "end": v(28.44, -12.83) * mm});
            skLineSegment(sketch, "E15.36.1", {"start": v(29.47, -5.62) * mm, "end": v(28.53, -9.27) * mm, "construction": true});
            skLineSegment(sketch, "E15.36.2", {"start": v(30.55, -6.34) * mm, "end": v(28.02, -6.68) * mm});
            skLineSegment(sketch, "E15.36.3", {"start": v(28.53, -9.27) * mm, "end": v(29.67, -9.64) * mm, "construction": true});
            skLineSegment(sketch, "E15.36.4", {"start": v(27.77, -7.65) * mm, "end": v(29.83, -9.17) * mm});
            skLineSegment(sketch, "E15.36.6", {"start": v(30.65, -5.85) * mm, "end": v(30.55, -6.34) * mm});
            skLineSegment(sketch, "E15.36.7", {"start": v(27.9, -7.16) * mm, "end": v(28.02, -6.68) * mm});
            skLineSegment(sketch, "E15.36.8", {"start": v(27.9, -7.16) * mm, "end": v(27.77, -7.65) * mm});
            skLineSegment(sketch, "E15.36.9", {"start": v(29.67, -9.64) * mm, "end": v(29.83, -9.17) * mm});
            skLineSegment(sketch, "E15.37.1", {"start": v(29.94, -1.88) * mm, "end": v(29.47, -5.62) * mm, "construction": true});
            skLineSegment(sketch, "E15.37.2", {"start": v(31.1, -2.46) * mm, "end": v(28.64, -3.11) * mm});
            skLineSegment(sketch, "E15.37.3", {"start": v(29.47, -5.62) * mm, "end": v(30.65, -5.85) * mm, "construction": true});
            skLineSegment(sketch, "E15.37.4", {"start": v(28.51, -4.1) * mm, "end": v(30.74, -5.36) * mm});
            skLineSegment(sketch, "E15.37.6", {"start": v(31.14, -1.96) * mm, "end": v(31.1, -2.46) * mm});
            skLineSegment(sketch, "E15.37.7", {"start": v(28.57, -3.6) * mm, "end": v(28.64, -3.11) * mm});
            skLineSegment(sketch, "E15.37.8", {"start": v(28.57, -3.6) * mm, "end": v(28.51, -4.1) * mm});
            skLineSegment(sketch, "E15.37.9", {"start": v(30.65, -5.85) * mm, "end": v(30.74, -5.36) * mm});
            skLineSegment(sketch, "E15.38.1", {"start": v(29.94, 1.88) * mm, "end": v(29.94, -1.88) * mm, "construction": true});
            skLineSegment(sketch, "E15.38.2", {"start": v(31.17, 1.46) * mm, "end": v(28.8, 0.5) * mm});
            skLineSegment(sketch, "E15.38.3", {"start": v(29.94, -1.88) * mm, "end": v(31.14, -1.96) * mm, "construction": true});
            skLineSegment(sketch, "E15.38.4", {"start": v(28.8, -0.5) * mm, "end": v(31.17, -1.46) * mm});
            skLineSegment(sketch, "E15.38.6", {"start": v(31.14, 1.96) * mm, "end": v(31.17, 1.46) * mm});
            skLineSegment(sketch, "E15.38.7", {"start": v(28.8, 0) * mm, "end": v(28.8, 0.5) * mm});
            skLineSegment(sketch, "E15.38.8", {"start": v(28.8, 0) * mm, "end": v(28.8, -0.5) * mm});
            skLineSegment(sketch, "E15.38.9", {"start": v(31.14, -1.96) * mm, "end": v(31.17, -1.46) * mm});
            skLineSegment(sketch, "E15.39.1", {"start": v(29.47, 5.62) * mm, "end": v(29.94, 1.88) * mm, "construction": true});
            skLineSegment(sketch, "E15.39.2", {"start": v(30.74, 5.36) * mm, "end": v(28.51, 4.1) * mm});
            skLineSegment(sketch, "E15.39.3", {"start": v(29.94, 1.88) * mm, "end": v(31.14, 1.96) * mm, "construction": true});
            skLineSegment(sketch, "E15.39.4", {"start": v(28.64, 3.11) * mm, "end": v(31.1, 2.46) * mm});
            skLineSegment(sketch, "E15.39.6", {"start": v(30.65, 5.85) * mm, "end": v(30.74, 5.36) * mm});
            skLineSegment(sketch, "E15.39.7", {"start": v(28.57, 3.6) * mm, "end": v(28.51, 4.1) * mm});
            skLineSegment(sketch, "E15.39.8", {"start": v(28.57, 3.6) * mm, "end": v(28.64, 3.11) * mm});
            skLineSegment(sketch, "E15.39.9", {"start": v(31.14, 1.96) * mm, "end": v(31.1, 2.46) * mm});
            skLineSegment(sketch, "E15.40.1", {"start": v(28.53, 9.27) * mm, "end": v(29.47, 5.62) * mm, "construction": true});
            skLineSegment(sketch, "E15.40.2", {"start": v(29.83, 9.17) * mm, "end": v(27.77, 7.65) * mm});
            skLineSegment(sketch, "E15.40.3", {"start": v(29.47, 5.62) * mm, "end": v(30.65, 5.85) * mm, "construction": true});
            skLineSegment(sketch, "E15.40.4", {"start": v(28.02, 6.68) * mm, "end": v(30.55, 6.34) * mm});
            skLineSegment(sketch, "E15.40.6", {"start": v(29.67, 9.64) * mm, "end": v(29.83, 9.17) * mm});
            skLineSegment(sketch, "E15.40.7", {"start": v(27.9, 7.16) * mm, "end": v(27.77, 7.65) * mm});
            skLineSegment(sketch, "E15.40.8", {"start": v(27.9, 7.16) * mm, "end": v(28.02, 6.68) * mm});
            skLineSegment(sketch, "E15.40.9", {"start": v(30.65, 5.85) * mm, "end": v(30.55, 6.34) * mm});
            skLineSegment(sketch, "E15.41.1", {"start": v(27.14, 12.77) * mm, "end": v(28.53, 9.27) * mm, "construction": true});
            skLineSegment(sketch, "E15.41.2", {"start": v(28.44, 12.83) * mm, "end": v(26.6, 11.07) * mm});
            skLineSegment(sketch, "E15.41.3", {"start": v(28.53, 9.27) * mm, "end": v(29.67, 9.64) * mm, "construction": true});
            skLineSegment(sketch, "E15.41.4", {"start": v(26.96, 10.14) * mm, "end": v(29.52, 10.12) * mm});
            skLineSegment(sketch, "E15.41.6", {"start": v(28.23, 13.28) * mm, "end": v(28.44, 12.83) * mm});
            skLineSegment(sketch, "E15.41.7", {"start": v(26.78, 10.6) * mm, "end": v(26.6, 11.07) * mm});
            skLineSegment(sketch, "E15.41.8", {"start": v(26.78, 10.6) * mm, "end": v(26.96, 10.14) * mm});
            skLineSegment(sketch, "E15.41.9", {"start": v(29.67, 9.64) * mm, "end": v(29.52, 10.12) * mm});
            skLineSegment(sketch, "E15.42.1", {"start": v(25.33, 16.07) * mm, "end": v(27.14, 12.77) * mm, "construction": true});
            skLineSegment(sketch, "E15.42.2", {"start": v(26.61, 16.3) * mm, "end": v(25, 14.31) * mm});
            skLineSegment(sketch, "E15.42.3", {"start": v(27.14, 12.77) * mm, "end": v(28.23, 13.28) * mm, "construction": true});
            skLineSegment(sketch, "E15.42.4", {"start": v(25.48, 13.44) * mm, "end": v(28.02, 13.74) * mm});
            skLineSegment(sketch, "E15.42.6", {"start": v(26.34, 16.72) * mm, "end": v(26.61, 16.3) * mm});
            skLineSegment(sketch, "E15.42.7", {"start": v(25.24, 13.87) * mm, "end": v(25, 14.31) * mm});
            skLineSegment(sketch, "E15.42.8", {"start": v(25.24, 13.87) * mm, "end": v(25.48, 13.44) * mm});
            skLineSegment(sketch, "E15.42.9", {"start": v(28.23, 13.28) * mm, "end": v(28.02, 13.74) * mm});
            skLineSegment(sketch, "E15.43.1", {"start": v(23.12, 19.12) * mm, "end": v(25.33, 16.07) * mm, "construction": true});
            skLineSegment(sketch, "E15.43.2", {"start": v(24.36, 19.5) * mm, "end": v(23, 17.33) * mm});
            skLineSegment(sketch, "E15.43.3", {"start": v(25.33, 16.07) * mm, "end": v(26.34, 16.72) * mm, "construction": true});
            skLineSegment(sketch, "E15.43.4", {"start": v(23.6, 16.52) * mm, "end": v(26.08, 17.14) * mm});
            skLineSegment(sketch, "E15.43.6", {"start": v(24.04, 19.89) * mm, "end": v(24.36, 19.5) * mm});
            skLineSegment(sketch, "E15.43.7", {"start": v(23.3, 16.93) * mm, "end": v(23, 17.33) * mm});
            skLineSegment(sketch, "E15.43.8", {"start": v(23.3, 16.93) * mm, "end": v(23.6, 16.52) * mm});
            skLineSegment(sketch, "E15.43.9", {"start": v(26.34, 16.72) * mm, "end": v(26.08, 17.14) * mm});
            skLineSegment(sketch, "E15.44.1", {"start": v(20.54, 21.87) * mm, "end": v(23.12, 19.12) * mm, "construction": true});
            skLineSegment(sketch, "E15.44.2", {"start": v(21.72, 22.4) * mm, "end": v(20.65, 20.08) * mm});
            skLineSegment(sketch, "E15.44.3", {"start": v(23.12, 19.12) * mm, "end": v(24.04, 19.89) * mm, "construction": true});
            skLineSegment(sketch, "E15.44.4", {"start": v(21.34, 19.35) * mm, "end": v(23.72, 20.27) * mm});
            skLineSegment(sketch, "E15.44.6", {"start": v(21.36, 22.74) * mm, "end": v(21.72, 22.4) * mm});
            skLineSegment(sketch, "E15.44.7", {"start": v(21, 19.71) * mm, "end": v(20.65, 20.08) * mm});
            skLineSegment(sketch, "E15.44.8", {"start": v(21, 19.71) * mm, "end": v(21.34, 19.35) * mm});
            skLineSegment(sketch, "E15.44.9", {"start": v(24.04, 19.89) * mm, "end": v(23.72, 20.27) * mm});
            skLineSegment(sketch, "E15.45.1", {"start": v(17.63, 24.27) * mm, "end": v(20.54, 21.87) * mm, "construction": true});
            skLineSegment(sketch, "E15.45.2", {"start": v(18.74, 24.95) * mm, "end": v(17.97, 22.5) * mm});
            skLineSegment(sketch, "E15.45.3", {"start": v(20.54, 21.87) * mm, "end": v(21.36, 22.74) * mm, "construction": true});
            skLineSegment(sketch, "E15.45.4", {"start": v(18.74, 21.87) * mm, "end": v(21, 23.09) * mm});
            skLineSegment(sketch, "E15.45.6", {"start": v(18.34, 25.24) * mm, "end": v(18.74, 24.95) * mm});
            skLineSegment(sketch, "E15.45.7", {"start": v(18.36, 22.2) * mm, "end": v(17.97, 22.5) * mm});
            skLineSegment(sketch, "E15.45.8", {"start": v(18.36, 22.2) * mm, "end": v(18.74, 21.87) * mm});
            skLineSegment(sketch, "E15.45.9", {"start": v(21.36, 22.74) * mm, "end": v(21, 23.09) * mm});
            skLineSegment(sketch, "E15.46.1", {"start": v(14.45, 26.29) * mm, "end": v(17.63, 24.27) * mm, "construction": true});
            skLineSegment(sketch, "E15.46.2", {"start": v(15.47, 27.1) * mm, "end": v(15, 24.58) * mm});
            skLineSegment(sketch, "E15.46.3", {"start": v(17.63, 24.27) * mm, "end": v(18.34, 25.24) * mm, "construction": true});
            skLineSegment(sketch, "E15.46.4", {"start": v(15.85, 24.05) * mm, "end": v(17.93, 25.54) * mm});
            skLineSegment(sketch, "E15.46.6", {"start": v(15.03, 27.34) * mm, "end": v(15.47, 27.1) * mm});
            skLineSegment(sketch, "E15.46.7", {"start": v(15.43, 24.32) * mm, "end": v(15, 24.58) * mm});
            skLineSegment(sketch, "E15.46.8", {"start": v(15.43, 24.32) * mm, "end": v(15.85, 24.05) * mm});
            skLineSegment(sketch, "E15.46.9", {"start": v(18.34, 25.24) * mm, "end": v(17.93, 25.54) * mm});
            skLineSegment(sketch, "E15.47.1", {"start": v(11.04, 27.9) * mm, "end": v(14.45, 26.29) * mm, "construction": true});
            skLineSegment(sketch, "E15.47.2", {"start": v(11.95, 28.82) * mm, "end": v(11.81, 26.27) * mm});
            skLineSegment(sketch, "E15.47.3", {"start": v(14.45, 26.29) * mm, "end": v(15.03, 27.34) * mm, "construction": true});
            skLineSegment(sketch, "E15.47.4", {"start": v(12.71, 25.85) * mm, "end": v(14.6, 27.58) * mm});
            skLineSegment(sketch, "E15.47.6", {"start": v(11.49, 29) * mm, "end": v(11.95, 28.82) * mm});
            skLineSegment(sketch, "E15.47.7", {"start": v(12.26, 26.06) * mm, "end": v(11.81, 26.27) * mm});
            skLineSegment(sketch, "E15.47.8", {"start": v(12.26, 26.06) * mm, "end": v(12.71, 25.85) * mm});
            skLineSegment(sketch, "E15.47.9", {"start": v(15.03, 27.34) * mm, "end": v(14.6, 27.58) * mm});
            skLineSegment(sketch, "E15.48.1", {"start": v(7.46, 29.06) * mm, "end": v(11.04, 27.9) * mm, "construction": true});
            skLineSegment(sketch, "E15.48.2", {"start": v(8.24, 30.1) * mm, "end": v(8.42, 27.54) * mm});
            skLineSegment(sketch, "E15.48.3", {"start": v(11.04, 27.9) * mm, "end": v(11.49, 29) * mm, "construction": true});
            skLineSegment(sketch, "E15.48.4", {"start": v(9.38, 27.24) * mm, "end": v(11.02, 29.2) * mm});
            skLineSegment(sketch, "E15.48.6", {"start": v(7.76, 30.22) * mm, "end": v(8.24, 30.1) * mm});
            skLineSegment(sketch, "E15.48.7", {"start": v(8.9, 27.4) * mm, "end": v(8.42, 27.54) * mm});
            skLineSegment(sketch, "E15.48.8", {"start": v(8.9, 27.4) * mm, "end": v(9.38, 27.24) * mm});
            skLineSegment(sketch, "E15.48.9", {"start": v(11.49, 29) * mm, "end": v(11.02, 29.2) * mm});
            skLineSegment(sketch, "E15.49.1", {"start": v(3.76, 29.76) * mm, "end": v(7.46, 29.06) * mm, "construction": true});
            skLineSegment(sketch, "E15.49.2", {"start": v(4.4, 30.9) * mm, "end": v(4.9, 28.38) * mm});
            skLineSegment(sketch, "E15.49.3", {"start": v(7.46, 29.06) * mm, "end": v(7.76, 30.22) * mm, "construction": true});
            skLineSegment(sketch, "E15.49.4", {"start": v(5.89, 28.2) * mm, "end": v(7.27, 30.34) * mm});
            skLineSegment(sketch, "E15.49.6", {"start": v(3.91, 30.95) * mm, "end": v(4.4, 30.9) * mm});
            skLineSegment(sketch, "E15.49.7", {"start": v(5.4, 28.29) * mm, "end": v(4.9, 28.38) * mm});
            skLineSegment(sketch, "E15.49.8", {"start": v(5.4, 28.29) * mm, "end": v(5.89, 28.2) * mm});
            skLineSegment(sketch, "E15.49.9", {"start": v(7.76, 30.22) * mm, "end": v(7.27, 30.34) * mm});
            skCircle(sketch, "E16", {"center": v(0, 0) * mm, "radius": 5.5 * mm});
            skSolve(sketch);
        }
        {
            var Q0;
            Q0 = qSketchRegion(id + "F0", true);
            extrude(context, id + "F1", {"entities" : qUnion([Q0]), "depth" : 5.8 * mm});
        }
        {
            var Q0;
            Q0=makeQuery(id+"F1.opExtrude","CAP_FACE",FACE,{"disambiguationData":[OSD([sQuery(id+"F0.wireOp",EDGE,"E7"),sQuery(id+"F0.wireOp",EDGE,"E8"),sQuery(id+"F0.wireOp",EDGE,"E9"),sQuery(id+"F0.wireOp",EDGE,"E11"),sQuery(id+"F0.wireOp",EDGE,"E13"),sQuery(id+"F0.wireOp",EDGE,"E14"),sQuery(id+"F0.wireOp",EDGE,"E15.1.2"),sQuery(id+"F0.wireOp",EDGE,"E15.1.4"),sQuery(id+"F0.wireOp",EDGE,"E15.1.6"),sQuery(id+"F0.wireOp",EDGE,"E15.1.7"),sQuery(id+"F0.wireOp",EDGE,"E15.1.8"),sQuery(id+"F0.wireOp",EDGE,"E15.1.9"),sQuery(id+"F0.wireOp",EDGE,"E15.2.2"),sQuery(id+"F0.wireOp",EDGE,"E15.2.4"),sQuery(id+"F0.wireOp",EDGE,"E15.2.6"),sQuery(id+"F0.wireOp",EDGE,"E15.2.7"),sQuery(id+"F0.wireOp",EDGE,"E15.2.8"),sQuery(id+"F0.wireOp",EDGE,"E15.2.9"),sQuery(id+"F0.wireOp",EDGE,"E15.3.2"),sQuery(id+"F0.wireOp",EDGE,"E15.3.4"),sQuery(id+"F0.wireOp",EDGE,"E15.3.6"),sQuery(id+"F0.wireOp",EDGE,"E15.3.7"),sQuery(id+"F0.wireOp",EDGE,"E15.3.8"),sQuery(id+"F0.wireOp",EDGE,"E15.3.9"),sQuery(id+"F0.wireOp",EDGE,"E15.4.2"),sQuery(id+"F0.wireOp",EDGE,"E15.4.4"),sQuery(id+"F0.wireOp",EDGE,"E15.4.6"),sQuery(id+"F0.wireOp",EDGE,"E15.4.7"),sQuery(id+"F0.wireOp",EDGE,"E15.4.8"),sQuery(id+"F0.wireOp",EDGE,"E15.4.9"),sQuery(id+"F0.wireOp",EDGE,"E15.5.2"),sQuery(id+"F0.wireOp",EDGE,"E15.5.4"),sQuery(id+"F0.wireOp",EDGE,"E15.5.6"),sQuery(id+"F0.wireOp",EDGE,"E15.5.7"),sQuery(id+"F0.wireOp",EDGE,"E15.5.8"),sQuery(id+"F0.wireOp",EDGE,"E15.5.9"),sQuery(id+"F0.wireOp",EDGE,"E15.6.2"),sQuery(id+"F0.wireOp",EDGE,"E15.6.4"),sQuery(id+"F0.wireOp",EDGE,"E15.6.6"),sQuery(id+"F0.wireOp",EDGE,"E15.6.7"),sQuery(id+"F0.wireOp",EDGE,"E15.6.8"),sQuery(id+"F0.wireOp",EDGE,"E15.6.9"),sQuery(id+"F0.wireOp",EDGE,"E15.7.2"),sQuery(id+"F0.wireOp",EDGE,"E15.7.4"),sQuery(id+"F0.wireOp",EDGE,"E15.7.6"),sQuery(id+"F0.wireOp",EDGE,"E15.7.7"),sQuery(id+"F0.wireOp",EDGE,"E15.7.8"),sQuery(id+"F0.wireOp",EDGE,"E15.7.9"),sQuery(id+"F0.wireOp",EDGE,"E15.8.2"),sQuery(id+"F0.wireOp",EDGE,"E15.8.4"),sQuery(id+"F0.wireOp",EDGE,"E15.8.6"),sQuery(id+"F0.wireOp",EDGE,"E15.8.7"),sQuery(id+"F0.wireOp",EDGE,"E15.8.8"),sQuery(id+"F0.wireOp",EDGE,"E15.8.9"),sQuery(id+"F0.wireOp",EDGE,"E15.9.2"),sQuery(id+"F0.wireOp",EDGE,"E15.9.4"),sQuery(id+"F0.wireOp",EDGE,"E15.9.6"),sQuery(id+"F0.wireOp",EDGE,"E15.9.7"),sQuery(id+"F0.wireOp",EDGE,"E15.9.8"),sQuery(id+"F0.wireOp",EDGE,"E15.9.9"),sQuery(id+"F0.wireOp",EDGE,"E15.10.2"),sQuery(id+"F0.wireOp",EDGE,"E15.10.4"),sQuery(id+"F0.wireOp",EDGE,"E15.10.6"),sQuery(id+"F0.wireOp",EDGE,"E15.10.7"),sQuery(id+"F0.wireOp",EDGE,"E15.10.8"),sQuery(id+"F0.wireOp",EDGE,"E15.10.9"),sQuery(id+"F0.wireOp",EDGE,"E15.11.2"),sQuery(id+"F0.wireOp",EDGE,"E15.11.4"),sQuery(id+"F0.wireOp",EDGE,"E15.11.6"),sQuery(id+"F0.wireOp",EDGE,"E15.11.7"),sQuery(id+"F0.wireOp",EDGE,"E15.11.8"),sQuery(id+"F0.wireOp",EDGE,"E15.11.9"),sQuery(id+"F0.wireOp",EDGE,"E15.12.2"),sQuery(id+"F0.wireOp",EDGE,"E15.12.4"),sQuery(id+"F0.wireOp",EDGE,"E15.12.6"),sQuery(id+"F0.wireOp",EDGE,"E15.12.7"),sQuery(id+"F0.wireOp",EDGE,"E15.12.8"),sQuery(id+"F0.wireOp",EDGE,"E15.12.9"),sQuery(id+"F0.wireOp",EDGE,"E15.13.2"),sQuery(id+"F0.wireOp",EDGE,"E15.13.4"),sQuery(id+"F0.wireOp",EDGE,"E15.13.6"),sQuery(id+"F0.wireOp",EDGE,"E15.13.7"),sQuery(id+"F0.wireOp",EDGE,"E15.13.8"),sQuery(id+"F0.wireOp",EDGE,"E15.13.9"),sQuery(id+"F0.wireOp",EDGE,"E15.14.2"),sQuery(id+"F0.wireOp",EDGE,"E15.14.4"),sQuery(id+"F0.wireOp",EDGE,"E15.14.6"),sQuery(id+"F0.wireOp",EDGE,"E15.14.7"),sQuery(id+"F0.wireOp",EDGE,"E15.14.8"),sQuery(id+"F0.wireOp",EDGE,"E15.14.9"),sQuery(id+"F0.wireOp",EDGE,"E15.15.2"),sQuery(id+"F0.wireOp",EDGE,"E15.15.4"),sQuery(id+"F0.wireOp",EDGE,"E15.15.6"),sQuery(id+"F0.wireOp",EDGE,"E15.15.7"),sQuery(id+"F0.wireOp",EDGE,"E15.15.8"),sQuery(id+"F0.wireOp",EDGE,"E15.15.9"),sQuery(id+"F0.wireOp",EDGE,"E15.16.2"),sQuery(id+"F0.wireOp",EDGE,"E15.16.4"),sQuery(id+"F0.wireOp",EDGE,"E15.16.6"),sQuery(id+"F0.wireOp",EDGE,"E15.16.7"),sQuery(id+"F0.wireOp",EDGE,"E15.16.8"),sQuery(id+"F0.wireOp",EDGE,"E15.16.9"),sQuery(id+"F0.wireOp",EDGE,"E15.17.2"),sQuery(id+"F0.wireOp",EDGE,"E15.17.4"),sQuery(id+"F0.wireOp",EDGE,"E15.17.6"),sQuery(id+"F0.wireOp",EDGE,"E15.17.7"),sQuery(id+"F0.wireOp",EDGE,"E15.17.8"),sQuery(id+"F0.wireOp",EDGE,"E15.17.9"),sQuery(id+"F0.wireOp",EDGE,"E15.18.2"),sQuery(id+"F0.wireOp",EDGE,"E15.18.4"),sQuery(id+"F0.wireOp",EDGE,"E15.18.6"),sQuery(id+"F0.wireOp",EDGE,"E15.18.7"),sQuery(id+"F0.wireOp",EDGE,"E15.18.8"),sQuery(id+"F0.wireOp",EDGE,"E15.18.9"),sQuery(id+"F0.wireOp",EDGE,"E15.19.2"),sQuery(id+"F0.wireOp",EDGE,"E15.19.4"),sQuery(id+"F0.wireOp",EDGE,"E15.19.6"),sQuery(id+"F0.wireOp",EDGE,"E15.19.7"),sQuery(id+"F0.wireOp",EDGE,"E15.19.8"),sQuery(id+"F0.wireOp",EDGE,"E15.19.9"),sQuery(id+"F0.wireOp",EDGE,"E15.20.2"),sQuery(id+"F0.wireOp",EDGE,"E15.20.4"),sQuery(id+"F0.wireOp",EDGE,"E15.20.6"),sQuery(id+"F0.wireOp",EDGE,"E15.20.7"),sQuery(id+"F0.wireOp",EDGE,"E15.20.8"),sQuery(id+"F0.wireOp",EDGE,"E15.20.9"),sQuery(id+"F0.wireOp",EDGE,"E15.21.2"),sQuery(id+"F0.wireOp",EDGE,"E15.21.4"),sQuery(id+"F0.wireOp",EDGE,"E15.21.6"),sQuery(id+"F0.wireOp",EDGE,"E15.21.7"),sQuery(id+"F0.wireOp",EDGE,"E15.21.8"),sQuery(id+"F0.wireOp",EDGE,"E15.21.9"),sQuery(id+"F0.wireOp",EDGE,"E15.22.2"),sQuery(id+"F0.wireOp",EDGE,"E15.22.4"),sQuery(id+"F0.wireOp",EDGE,"E15.22.6"),sQuery(id+"F0.wireOp",EDGE,"E15.22.7"),sQuery(id+"F0.wireOp",EDGE,"E15.22.8"),sQuery(id+"F0.wireOp",EDGE,"E15.22.9"),sQuery(id+"F0.wireOp",EDGE,"E15.23.2"),sQuery(id+"F0.wireOp",EDGE,"E15.23.4"),sQuery(id+"F0.wireOp",EDGE,"E15.23.6"),sQuery(id+"F0.wireOp",EDGE,"E15.23.7"),sQuery(id+"F0.wireOp",EDGE,"E15.23.8"),sQuery(id+"F0.wireOp",EDGE,"E15.23.9"),sQuery(id+"F0.wireOp",EDGE,"E15.24.2"),sQuery(id+"F0.wireOp",EDGE,"E15.24.4"),sQuery(id+"F0.wireOp",EDGE,"E15.24.6"),sQuery(id+"F0.wireOp",EDGE,"E15.24.7"),sQuery(id+"F0.wireOp",EDGE,"E15.24.8"),sQuery(id+"F0.wireOp",EDGE,"E15.24.9"),sQuery(id+"F0.wireOp",EDGE,"E15.25.2"),sQuery(id+"F0.wireOp",EDGE,"E15.25.4"),sQuery(id+"F0.wireOp",EDGE,"E15.25.6"),sQuery(id+"F0.wireOp",EDGE,"E15.25.7"),sQuery(id+"F0.wireOp",EDGE,"E15.25.8"),sQuery(id+"F0.wireOp",EDGE,"E15.25.9"),sQuery(id+"F0.wireOp",EDGE,"E15.26.2"),sQuery(id+"F0.wireOp",EDGE,"E15.26.4"),sQuery(id+"F0.wireOp",EDGE,"E15.26.6"),sQuery(id+"F0.wireOp",EDGE,"E15.26.7"),sQuery(id+"F0.wireOp",EDGE,"E15.26.8"),sQuery(id+"F0.wireOp",EDGE,"E15.26.9"),sQuery(id+"F0.wireOp",EDGE,"E15.27.2"),sQuery(id+"F0.wireOp",EDGE,"E15.27.4"),sQuery(id+"F0.wireOp",EDGE,"E15.27.6"),sQuery(id+"F0.wireOp",EDGE,"E15.27.7"),sQuery(id+"F0.wireOp",EDGE,"E15.27.8"),sQuery(id+"F0.wireOp",EDGE,"E15.27.9"),sQuery(id+"F0.wireOp",EDGE,"E15.28.2"),sQuery(id+"F0.wireOp",EDGE,"E15.28.4"),sQuery(id+"F0.wireOp",EDGE,"E15.28.6"),sQuery(id+"F0.wireOp",EDGE,"E15.28.7"),sQuery(id+"F0.wireOp",EDGE,"E15.28.8"),sQuery(id+"F0.wireOp",EDGE,"E15.28.9"),sQuery(id+"F0.wireOp",EDGE,"E15.29.2"),sQuery(id+"F0.wireOp",EDGE,"E15.29.4"),sQuery(id+"F0.wireOp",EDGE,"E15.29.6"),sQuery(id+"F0.wireOp",EDGE,"E15.29.7"),sQuery(id+"F0.wireOp",EDGE,"E15.29.8"),sQuery(id+"F0.wireOp",EDGE,"E15.29.9"),sQuery(id+"F0.wireOp",EDGE,"E15.30.2"),sQuery(id+"F0.wireOp",EDGE,"E15.30.4"),sQuery(id+"F0.wireOp",EDGE,"E15.30.6"),sQuery(id+"F0.wireOp",EDGE,"E15.30.7"),sQuery(id+"F0.wireOp",EDGE,"E15.30.8"),sQuery(id+"F0.wireOp",EDGE,"E15.30.9"),sQuery(id+"F0.wireOp",EDGE,"E15.31.2"),sQuery(id+"F0.wireOp",EDGE,"E15.31.4"),sQuery(id+"F0.wireOp",EDGE,"E15.31.6"),sQuery(id+"F0.wireOp",EDGE,"E15.31.7"),sQuery(id+"F0.wireOp",EDGE,"E15.31.8"),sQuery(id+"F0.wireOp",EDGE,"E15.31.9"),sQuery(id+"F0.wireOp",EDGE,"E15.32.2"),sQuery(id+"F0.wireOp",EDGE,"E15.32.4"),sQuery(id+"F0.wireOp",EDGE,"E15.32.6"),sQuery(id+"F0.wireOp",EDGE,"E15.32.7"),sQuery(id+"F0.wireOp",EDGE,"E15.32.8"),sQuery(id+"F0.wireOp",EDGE,"E15.32.9"),sQuery(id+"F0.wireOp",EDGE,"E15.33.2"),sQuery(id+"F0.wireOp",EDGE,"E15.33.4"),sQuery(id+"F0.wireOp",EDGE,"E15.33.6"),sQuery(id+"F0.wireOp",EDGE,"E15.33.7"),sQuery(id+"F0.wireOp",EDGE,"E15.33.8"),sQuery(id+"F0.wireOp",EDGE,"E15.33.9"),sQuery(id+"F0.wireOp",EDGE,"E15.34.2"),sQuery(id+"F0.wireOp",EDGE,"E15.34.4"),sQuery(id+"F0.wireOp",EDGE,"E15.34.6"),sQuery(id+"F0.wireOp",EDGE,"E15.34.7"),sQuery(id+"F0.wireOp",EDGE,"E15.34.8"),sQuery(id+"F0.wireOp",EDGE,"E15.34.9"),sQuery(id+"F0.wireOp",EDGE,"E15.35.2"),sQuery(id+"F0.wireOp",EDGE,"E15.35.4"),sQuery(id+"F0.wireOp",EDGE,"E15.35.6"),sQuery(id+"F0.wireOp",EDGE,"E15.35.7"),sQuery(id+"F0.wireOp",EDGE,"E15.35.8"),sQuery(id+"F0.wireOp",EDGE,"E15.35.9"),sQuery(id+"F0.wireOp",EDGE,"E15.36.2"),sQuery(id+"F0.wireOp",EDGE,"E15.36.4"),sQuery(id+"F0.wireOp",EDGE,"E15.36.6"),sQuery(id+"F0.wireOp",EDGE,"E15.36.7"),sQuery(id+"F0.wireOp",EDGE,"E15.36.8"),sQuery(id+"F0.wireOp",EDGE,"E15.36.9"),sQuery(id+"F0.wireOp",EDGE,"E15.37.2"),sQuery(id+"F0.wireOp",EDGE,"E15.37.4"),sQuery(id+"F0.wireOp",EDGE,"E15.37.6"),sQuery(id+"F0.wireOp",EDGE,"E15.37.7"),sQuery(id+"F0.wireOp",EDGE,"E15.37.8"),sQuery(id+"F0.wireOp",EDGE,"E15.37.9"),sQuery(id+"F0.wireOp",EDGE,"E15.38.2"),sQuery(id+"F0.wireOp",EDGE,"E15.38.4"),sQuery(id+"F0.wireOp",EDGE,"E15.38.6"),sQuery(id+"F0.wireOp",EDGE,"E15.38.7"),sQuery(id+"F0.wireOp",EDGE,"E15.38.8"),sQuery(id+"F0.wireOp",EDGE,"E15.38.9"),sQuery(id+"F0.wireOp",EDGE,"E15.39.2"),sQuery(id+"F0.wireOp",EDGE,"E15.39.4"),sQuery(id+"F0.wireOp",EDGE,"E15.39.6"),sQuery(id+"F0.wireOp",EDGE,"E15.39.7"),sQuery(id+"F0.wireOp",EDGE,"E15.39.8"),sQuery(id+"F0.wireOp",EDGE,"E15.39.9"),sQuery(id+"F0.wireOp",EDGE,"E15.40.2"),sQuery(id+"F0.wireOp",EDGE,"E15.40.4"),sQuery(id+"F0.wireOp",EDGE,"E15.40.6"),sQuery(id+"F0.wireOp",EDGE,"E15.40.7"),sQuery(id+"F0.wireOp",EDGE,"E15.40.8"),sQuery(id+"F0.wireOp",EDGE,"E15.40.9"),sQuery(id+"F0.wireOp",EDGE,"E15.41.2"),sQuery(id+"F0.wireOp",EDGE,"E15.41.4"),sQuery(id+"F0.wireOp",EDGE,"E15.41.6"),sQuery(id+"F0.wireOp",EDGE,"E15.41.7"),sQuery(id+"F0.wireOp",EDGE,"E15.41.8"),sQuery(id+"F0.wireOp",EDGE,"E15.41.9"),sQuery(id+"F0.wireOp",EDGE,"E15.42.2"),sQuery(id+"F0.wireOp",EDGE,"E15.42.4"),sQuery(id+"F0.wireOp",EDGE,"E15.42.6"),sQuery(id+"F0.wireOp",EDGE,"E15.42.7"),sQuery(id+"F0.wireOp",EDGE,"E15.42.8"),sQuery(id+"F0.wireOp",EDGE,"E15.42.9"),sQuery(id+"F0.wireOp",EDGE,"E15.43.2"),sQuery(id+"F0.wireOp",EDGE,"E15.43.4"),sQuery(id+"F0.wireOp",EDGE,"E15.43.6"),sQuery(id+"F0.wireOp",EDGE,"E15.43.7"),sQuery(id+"F0.wireOp",EDGE,"E15.43.8"),sQuery(id+"F0.wireOp",EDGE,"E15.43.9"),sQuery(id+"F0.wireOp",EDGE,"E15.44.2"),sQuery(id+"F0.wireOp",EDGE,"E15.44.4"),sQuery(id+"F0.wireOp",EDGE,"E15.44.6"),sQuery(id+"F0.wireOp",EDGE,"E15.44.7"),sQuery(id+"F0.wireOp",EDGE,"E15.44.8"),sQuery(id+"F0.wireOp",EDGE,"E15.44.9"),sQuery(id+"F0.wireOp",EDGE,"E15.45.2"),sQuery(id+"F0.wireOp",EDGE,"E15.45.4"),sQuery(id+"F0.wireOp",EDGE,"E15.45.6"),sQuery(id+"F0.wireOp",EDGE,"E15.45.7"),sQuery(id+"F0.wireOp",EDGE,"E15.45.8"),sQuery(id+"F0.wireOp",EDGE,"E15.45.9"),sQuery(id+"F0.wireOp",EDGE,"E15.46.2"),sQuery(id+"F0.wireOp",EDGE,"E15.46.4"),sQuery(id+"F0.wireOp",EDGE,"E15.46.6"),sQuery(id+"F0.wireOp",EDGE,"E15.46.7"),sQuery(id+"F0.wireOp",EDGE,"E15.46.8"),sQuery(id+"F0.wireOp",EDGE,"E15.46.9"),sQuery(id+"F0.wireOp",EDGE,"E15.47.2"),sQuery(id+"F0.wireOp",EDGE,"E15.47.4"),sQuery(id+"F0.wireOp",EDGE,"E15.47.6"),sQuery(id+"F0.wireOp",EDGE,"E15.47.7"),sQuery(id+"F0.wireOp",EDGE,"E15.47.8"),sQuery(id+"F0.wireOp",EDGE,"E15.47.9"),sQuery(id+"F0.wireOp",EDGE,"E15.48.2"),sQuery(id+"F0.wireOp",EDGE,"E15.48.4"),sQuery(id+"F0.wireOp",EDGE,"E15.48.6"),sQuery(id+"F0.wireOp",EDGE,"E15.48.7"),sQuery(id+"F0.wireOp",EDGE,"E15.48.8"),sQuery(id+"F0.wireOp",EDGE,"E15.48.9"),sQuery(id+"F0.wireOp",EDGE,"E15.49.2"),sQuery(id+"F0.wireOp",EDGE,"E15.49.4"),sQuery(id+"F0.wireOp",EDGE,"E15.49.6"),sQuery(id+"F0.wireOp",EDGE,"E15.49.7"),sQuery(id+"F0.wireOp",EDGE,"E15.49.8"),sQuery(id+"F0.wireOp",EDGE,"E15.49.9"),sQuery(id+"F0.wireOp",EDGE,"E16")])],"isStart":false});
            var sketch = newSketch(context, id + "F2", { "sketchPlane" : qUnion([Q0])});
            skCircle(sketch, "E17.0", {"center": v(0, 0) * mm, "radius": 5.5 * mm, "construction": true});
            skLineSegment(sketch, "E18", {"start": v(0, 0) * mm, "end": v(5.5, 0) * mm, "construction": true});
            skLineSegment(sketch, "E19", {"start": v(5.5, 0) * mm, "end": v(5.5, 8) * mm});
            skLineSegment(sketch, "E20", {"start": v(5.5, 8) * mm, "end": v(8.5, 8) * mm});
            skLineSegment(sketch, "E21", {"start": v(8.5, 8) * mm, "end": v(8.5, 10) * mm});
            skLineSegment(sketch, "E22", {"start": v(8.5, 10) * mm, "end": v(3.5, 10) * mm});
            skLineSegment(sketch, "E23", {"start": v(3.5, 10) * mm, "end": v(3.5, 0) * mm});
            skLineSegment(sketch, "E24", {"start": v(3.5, 0) * mm, "end": v(5.5, 0) * mm});
            skSolve(sketch);
        }
        {
            var Q0;
            Q0 = qSketchRegion(id + "F2", true);
            var Q1;
            Q1=makeQuery(id+"F1.opExtrude","CAP_FACE",FACE,{"disambiguationData":[OSD([sQuery(id+"F0.wireOp",EDGE,"E7"),sQuery(id+"F0.wireOp",EDGE,"E8"),sQuery(id+"F0.wireOp",EDGE,"E9"),sQuery(id+"F0.wireOp",EDGE,"E11"),sQuery(id+"F0.wireOp",EDGE,"E13"),sQuery(id+"F0.wireOp",EDGE,"E14"),sQuery(id+"F0.wireOp",EDGE,"E15.1.2"),sQuery(id+"F0.wireOp",EDGE,"E15.1.4"),sQuery(id+"F0.wireOp",EDGE,"E15.1.6"),sQuery(id+"F0.wireOp",EDGE,"E15.1.7"),sQuery(id+"F0.wireOp",EDGE,"E15.1.8"),sQuery(id+"F0.wireOp",EDGE,"E15.1.9"),sQuery(id+"F0.wireOp",EDGE,"E15.2.2"),sQuery(id+"F0.wireOp",EDGE,"E15.2.4"),sQuery(id+"F0.wireOp",EDGE,"E15.2.6"),sQuery(id+"F0.wireOp",EDGE,"E15.2.7"),sQuery(id+"F0.wireOp",EDGE,"E15.2.8"),sQuery(id+"F0.wireOp",EDGE,"E15.2.9"),sQuery(id+"F0.wireOp",EDGE,"E15.3.2"),sQuery(id+"F0.wireOp",EDGE,"E15.3.4"),sQuery(id+"F0.wireOp",EDGE,"E15.3.6"),sQuery(id+"F0.wireOp",EDGE,"E15.3.7"),sQuery(id+"F0.wireOp",EDGE,"E15.3.8"),sQuery(id+"F0.wireOp",EDGE,"E15.3.9"),sQuery(id+"F0.wireOp",EDGE,"E15.4.2"),sQuery(id+"F0.wireOp",EDGE,"E15.4.4"),sQuery(id+"F0.wireOp",EDGE,"E15.4.6"),sQuery(id+"F0.wireOp",EDGE,"E15.4.7"),sQuery(id+"F0.wireOp",EDGE,"E15.4.8"),sQuery(id+"F0.wireOp",EDGE,"E15.4.9"),sQuery(id+"F0.wireOp",EDGE,"E15.5.2"),sQuery(id+"F0.wireOp",EDGE,"E15.5.4"),sQuery(id+"F0.wireOp",EDGE,"E15.5.6"),sQuery(id+"F0.wireOp",EDGE,"E15.5.7"),sQuery(id+"F0.wireOp",EDGE,"E15.5.8"),sQuery(id+"F0.wireOp",EDGE,"E15.5.9"),sQuery(id+"F0.wireOp",EDGE,"E15.6.2"),sQuery(id+"F0.wireOp",EDGE,"E15.6.4"),sQuery(id+"F0.wireOp",EDGE,"E15.6.6"),sQuery(id+"F0.wireOp",EDGE,"E15.6.7"),sQuery(id+"F0.wireOp",EDGE,"E15.6.8"),sQuery(id+"F0.wireOp",EDGE,"E15.6.9"),sQuery(id+"F0.wireOp",EDGE,"E15.7.2"),sQuery(id+"F0.wireOp",EDGE,"E15.7.4"),sQuery(id+"F0.wireOp",EDGE,"E15.7.6"),sQuery(id+"F0.wireOp",EDGE,"E15.7.7"),sQuery(id+"F0.wireOp",EDGE,"E15.7.8"),sQuery(id+"F0.wireOp",EDGE,"E15.7.9"),sQuery(id+"F0.wireOp",EDGE,"E15.8.2"),sQuery(id+"F0.wireOp",EDGE,"E15.8.4"),sQuery(id+"F0.wireOp",EDGE,"E15.8.6"),sQuery(id+"F0.wireOp",EDGE,"E15.8.7"),sQuery(id+"F0.wireOp",EDGE,"E15.8.8"),sQuery(id+"F0.wireOp",EDGE,"E15.8.9"),sQuery(id+"F0.wireOp",EDGE,"E15.9.2"),sQuery(id+"F0.wireOp",EDGE,"E15.9.4"),sQuery(id+"F0.wireOp",EDGE,"E15.9.6"),sQuery(id+"F0.wireOp",EDGE,"E15.9.7"),sQuery(id+"F0.wireOp",EDGE,"E15.9.8"),sQuery(id+"F0.wireOp",EDGE,"E15.9.9"),sQuery(id+"F0.wireOp",EDGE,"E15.10.2"),sQuery(id+"F0.wireOp",EDGE,"E15.10.4"),sQuery(id+"F0.wireOp",EDGE,"E15.10.6"),sQuery(id+"F0.wireOp",EDGE,"E15.10.7"),sQuery(id+"F0.wireOp",EDGE,"E15.10.8"),sQuery(id+"F0.wireOp",EDGE,"E15.10.9"),sQuery(id+"F0.wireOp",EDGE,"E15.11.2"),sQuery(id+"F0.wireOp",EDGE,"E15.11.4"),sQuery(id+"F0.wireOp",EDGE,"E15.11.6"),sQuery(id+"F0.wireOp",EDGE,"E15.11.7"),sQuery(id+"F0.wireOp",EDGE,"E15.11.8"),sQuery(id+"F0.wireOp",EDGE,"E15.11.9"),sQuery(id+"F0.wireOp",EDGE,"E15.12.2"),sQuery(id+"F0.wireOp",EDGE,"E15.12.4"),sQuery(id+"F0.wireOp",EDGE,"E15.12.6"),sQuery(id+"F0.wireOp",EDGE,"E15.12.7"),sQuery(id+"F0.wireOp",EDGE,"E15.12.8"),sQuery(id+"F0.wireOp",EDGE,"E15.12.9"),sQuery(id+"F0.wireOp",EDGE,"E15.13.2"),sQuery(id+"F0.wireOp",EDGE,"E15.13.4"),sQuery(id+"F0.wireOp",EDGE,"E15.13.6"),sQuery(id+"F0.wireOp",EDGE,"E15.13.7"),sQuery(id+"F0.wireOp",EDGE,"E15.13.8"),sQuery(id+"F0.wireOp",EDGE,"E15.13.9"),sQuery(id+"F0.wireOp",EDGE,"E15.14.2"),sQuery(id+"F0.wireOp",EDGE,"E15.14.4"),sQuery(id+"F0.wireOp",EDGE,"E15.14.6"),sQuery(id+"F0.wireOp",EDGE,"E15.14.7"),sQuery(id+"F0.wireOp",EDGE,"E15.14.8"),sQuery(id+"F0.wireOp",EDGE,"E15.14.9"),sQuery(id+"F0.wireOp",EDGE,"E15.15.2"),sQuery(id+"F0.wireOp",EDGE,"E15.15.4"),sQuery(id+"F0.wireOp",EDGE,"E15.15.6"),sQuery(id+"F0.wireOp",EDGE,"E15.15.7"),sQuery(id+"F0.wireOp",EDGE,"E15.15.8"),sQuery(id+"F0.wireOp",EDGE,"E15.15.9"),sQuery(id+"F0.wireOp",EDGE,"E15.16.2"),sQuery(id+"F0.wireOp",EDGE,"E15.16.4"),sQuery(id+"F0.wireOp",EDGE,"E15.16.6"),sQuery(id+"F0.wireOp",EDGE,"E15.16.7"),sQuery(id+"F0.wireOp",EDGE,"E15.16.8"),sQuery(id+"F0.wireOp",EDGE,"E15.16.9"),sQuery(id+"F0.wireOp",EDGE,"E15.17.2"),sQuery(id+"F0.wireOp",EDGE,"E15.17.4"),sQuery(id+"F0.wireOp",EDGE,"E15.17.6"),sQuery(id+"F0.wireOp",EDGE,"E15.17.7"),sQuery(id+"F0.wireOp",EDGE,"E15.17.8"),sQuery(id+"F0.wireOp",EDGE,"E15.17.9"),sQuery(id+"F0.wireOp",EDGE,"E15.18.2"),sQuery(id+"F0.wireOp",EDGE,"E15.18.4"),sQuery(id+"F0.wireOp",EDGE,"E15.18.6"),sQuery(id+"F0.wireOp",EDGE,"E15.18.7"),sQuery(id+"F0.wireOp",EDGE,"E15.18.8"),sQuery(id+"F0.wireOp",EDGE,"E15.18.9"),sQuery(id+"F0.wireOp",EDGE,"E15.19.2"),sQuery(id+"F0.wireOp",EDGE,"E15.19.4"),sQuery(id+"F0.wireOp",EDGE,"E15.19.6"),sQuery(id+"F0.wireOp",EDGE,"E15.19.7"),sQuery(id+"F0.wireOp",EDGE,"E15.19.8"),sQuery(id+"F0.wireOp",EDGE,"E15.19.9"),sQuery(id+"F0.wireOp",EDGE,"E15.20.2"),sQuery(id+"F0.wireOp",EDGE,"E15.20.4"),sQuery(id+"F0.wireOp",EDGE,"E15.20.6"),sQuery(id+"F0.wireOp",EDGE,"E15.20.7"),sQuery(id+"F0.wireOp",EDGE,"E15.20.8"),sQuery(id+"F0.wireOp",EDGE,"E15.20.9"),sQuery(id+"F0.wireOp",EDGE,"E15.21.2"),sQuery(id+"F0.wireOp",EDGE,"E15.21.4"),sQuery(id+"F0.wireOp",EDGE,"E15.21.6"),sQuery(id+"F0.wireOp",EDGE,"E15.21.7"),sQuery(id+"F0.wireOp",EDGE,"E15.21.8"),sQuery(id+"F0.wireOp",EDGE,"E15.21.9"),sQuery(id+"F0.wireOp",EDGE,"E15.22.2"),sQuery(id+"F0.wireOp",EDGE,"E15.22.4"),sQuery(id+"F0.wireOp",EDGE,"E15.22.6"),sQuery(id+"F0.wireOp",EDGE,"E15.22.7"),sQuery(id+"F0.wireOp",EDGE,"E15.22.8"),sQuery(id+"F0.wireOp",EDGE,"E15.22.9"),sQuery(id+"F0.wireOp",EDGE,"E15.23.2"),sQuery(id+"F0.wireOp",EDGE,"E15.23.4"),sQuery(id+"F0.wireOp",EDGE,"E15.23.6"),sQuery(id+"F0.wireOp",EDGE,"E15.23.7"),sQuery(id+"F0.wireOp",EDGE,"E15.23.8"),sQuery(id+"F0.wireOp",EDGE,"E15.23.9"),sQuery(id+"F0.wireOp",EDGE,"E15.24.2"),sQuery(id+"F0.wireOp",EDGE,"E15.24.4"),sQuery(id+"F0.wireOp",EDGE,"E15.24.6"),sQuery(id+"F0.wireOp",EDGE,"E15.24.7"),sQuery(id+"F0.wireOp",EDGE,"E15.24.8"),sQuery(id+"F0.wireOp",EDGE,"E15.24.9"),sQuery(id+"F0.wireOp",EDGE,"E15.25.2"),sQuery(id+"F0.wireOp",EDGE,"E15.25.4"),sQuery(id+"F0.wireOp",EDGE,"E15.25.6"),sQuery(id+"F0.wireOp",EDGE,"E15.25.7"),sQuery(id+"F0.wireOp",EDGE,"E15.25.8"),sQuery(id+"F0.wireOp",EDGE,"E15.25.9"),sQuery(id+"F0.wireOp",EDGE,"E15.26.2"),sQuery(id+"F0.wireOp",EDGE,"E15.26.4"),sQuery(id+"F0.wireOp",EDGE,"E15.26.6"),sQuery(id+"F0.wireOp",EDGE,"E15.26.7"),sQuery(id+"F0.wireOp",EDGE,"E15.26.8"),sQuery(id+"F0.wireOp",EDGE,"E15.26.9"),sQuery(id+"F0.wireOp",EDGE,"E15.27.2"),sQuery(id+"F0.wireOp",EDGE,"E15.27.4"),sQuery(id+"F0.wireOp",EDGE,"E15.27.6"),sQuery(id+"F0.wireOp",EDGE,"E15.27.7"),sQuery(id+"F0.wireOp",EDGE,"E15.27.8"),sQuery(id+"F0.wireOp",EDGE,"E15.27.9"),sQuery(id+"F0.wireOp",EDGE,"E15.28.2"),sQuery(id+"F0.wireOp",EDGE,"E15.28.4"),sQuery(id+"F0.wireOp",EDGE,"E15.28.6"),sQuery(id+"F0.wireOp",EDGE,"E15.28.7"),sQuery(id+"F0.wireOp",EDGE,"E15.28.8"),sQuery(id+"F0.wireOp",EDGE,"E15.28.9"),sQuery(id+"F0.wireOp",EDGE,"E15.29.2"),sQuery(id+"F0.wireOp",EDGE,"E15.29.4"),sQuery(id+"F0.wireOp",EDGE,"E15.29.6"),sQuery(id+"F0.wireOp",EDGE,"E15.29.7"),sQuery(id+"F0.wireOp",EDGE,"E15.29.8"),sQuery(id+"F0.wireOp",EDGE,"E15.29.9"),sQuery(id+"F0.wireOp",EDGE,"E15.30.2"),sQuery(id+"F0.wireOp",EDGE,"E15.30.4"),sQuery(id+"F0.wireOp",EDGE,"E15.30.6"),sQuery(id+"F0.wireOp",EDGE,"E15.30.7"),sQuery(id+"F0.wireOp",EDGE,"E15.30.8"),sQuery(id+"F0.wireOp",EDGE,"E15.30.9"),sQuery(id+"F0.wireOp",EDGE,"E15.31.2"),sQuery(id+"F0.wireOp",EDGE,"E15.31.4"),sQuery(id+"F0.wireOp",EDGE,"E15.31.6"),sQuery(id+"F0.wireOp",EDGE,"E15.31.7"),sQuery(id+"F0.wireOp",EDGE,"E15.31.8"),sQuery(id+"F0.wireOp",EDGE,"E15.31.9"),sQuery(id+"F0.wireOp",EDGE,"E15.32.2"),sQuery(id+"F0.wireOp",EDGE,"E15.32.4"),sQuery(id+"F0.wireOp",EDGE,"E15.32.6"),sQuery(id+"F0.wireOp",EDGE,"E15.32.7"),sQuery(id+"F0.wireOp",EDGE,"E15.32.8"),sQuery(id+"F0.wireOp",EDGE,"E15.32.9"),sQuery(id+"F0.wireOp",EDGE,"E15.33.2"),sQuery(id+"F0.wireOp",EDGE,"E15.33.4"),sQuery(id+"F0.wireOp",EDGE,"E15.33.6"),sQuery(id+"F0.wireOp",EDGE,"E15.33.7"),sQuery(id+"F0.wireOp",EDGE,"E15.33.8"),sQuery(id+"F0.wireOp",EDGE,"E15.33.9"),sQuery(id+"F0.wireOp",EDGE,"E15.34.2"),sQuery(id+"F0.wireOp",EDGE,"E15.34.4"),sQuery(id+"F0.wireOp",EDGE,"E15.34.6"),sQuery(id+"F0.wireOp",EDGE,"E15.34.7"),sQuery(id+"F0.wireOp",EDGE,"E15.34.8"),sQuery(id+"F0.wireOp",EDGE,"E15.34.9"),sQuery(id+"F0.wireOp",EDGE,"E15.35.2"),sQuery(id+"F0.wireOp",EDGE,"E15.35.4"),sQuery(id+"F0.wireOp",EDGE,"E15.35.6"),sQuery(id+"F0.wireOp",EDGE,"E15.35.7"),sQuery(id+"F0.wireOp",EDGE,"E15.35.8"),sQuery(id+"F0.wireOp",EDGE,"E15.35.9"),sQuery(id+"F0.wireOp",EDGE,"E15.36.2"),sQuery(id+"F0.wireOp",EDGE,"E15.36.4"),sQuery(id+"F0.wireOp",EDGE,"E15.36.6"),sQuery(id+"F0.wireOp",EDGE,"E15.36.7"),sQuery(id+"F0.wireOp",EDGE,"E15.36.8"),sQuery(id+"F0.wireOp",EDGE,"E15.36.9"),sQuery(id+"F0.wireOp",EDGE,"E15.37.2"),sQuery(id+"F0.wireOp",EDGE,"E15.37.4"),sQuery(id+"F0.wireOp",EDGE,"E15.37.6"),sQuery(id+"F0.wireOp",EDGE,"E15.37.7"),sQuery(id+"F0.wireOp",EDGE,"E15.37.8"),sQuery(id+"F0.wireOp",EDGE,"E15.37.9"),sQuery(id+"F0.wireOp",EDGE,"E15.38.2"),sQuery(id+"F0.wireOp",EDGE,"E15.38.4"),sQuery(id+"F0.wireOp",EDGE,"E15.38.6"),sQuery(id+"F0.wireOp",EDGE,"E15.38.7"),sQuery(id+"F0.wireOp",EDGE,"E15.38.8"),sQuery(id+"F0.wireOp",EDGE,"E15.38.9"),sQuery(id+"F0.wireOp",EDGE,"E15.39.2"),sQuery(id+"F0.wireOp",EDGE,"E15.39.4"),sQuery(id+"F0.wireOp",EDGE,"E15.39.6"),sQuery(id+"F0.wireOp",EDGE,"E15.39.7"),sQuery(id+"F0.wireOp",EDGE,"E15.39.8"),sQuery(id+"F0.wireOp",EDGE,"E15.39.9"),sQuery(id+"F0.wireOp",EDGE,"E15.40.2"),sQuery(id+"F0.wireOp",EDGE,"E15.40.4"),sQuery(id+"F0.wireOp",EDGE,"E15.40.6"),sQuery(id+"F0.wireOp",EDGE,"E15.40.7"),sQuery(id+"F0.wireOp",EDGE,"E15.40.8"),sQuery(id+"F0.wireOp",EDGE,"E15.40.9"),sQuery(id+"F0.wireOp",EDGE,"E15.41.2"),sQuery(id+"F0.wireOp",EDGE,"E15.41.4"),sQuery(id+"F0.wireOp",EDGE,"E15.41.6"),sQuery(id+"F0.wireOp",EDGE,"E15.41.7"),sQuery(id+"F0.wireOp",EDGE,"E15.41.8"),sQuery(id+"F0.wireOp",EDGE,"E15.41.9"),sQuery(id+"F0.wireOp",EDGE,"E15.42.2"),sQuery(id+"F0.wireOp",EDGE,"E15.42.4"),sQuery(id+"F0.wireOp",EDGE,"E15.42.6"),sQuery(id+"F0.wireOp",EDGE,"E15.42.7"),sQuery(id+"F0.wireOp",EDGE,"E15.42.8"),sQuery(id+"F0.wireOp",EDGE,"E15.42.9"),sQuery(id+"F0.wireOp",EDGE,"E15.43.2"),sQuery(id+"F0.wireOp",EDGE,"E15.43.4"),sQuery(id+"F0.wireOp",EDGE,"E15.43.6"),sQuery(id+"F0.wireOp",EDGE,"E15.43.7"),sQuery(id+"F0.wireOp",EDGE,"E15.43.8"),sQuery(id+"F0.wireOp",EDGE,"E15.43.9"),sQuery(id+"F0.wireOp",EDGE,"E15.44.2"),sQuery(id+"F0.wireOp",EDGE,"E15.44.4"),sQuery(id+"F0.wireOp",EDGE,"E15.44.6"),sQuery(id+"F0.wireOp",EDGE,"E15.44.7"),sQuery(id+"F0.wireOp",EDGE,"E15.44.8"),sQuery(id+"F0.wireOp",EDGE,"E15.44.9"),sQuery(id+"F0.wireOp",EDGE,"E15.45.2"),sQuery(id+"F0.wireOp",EDGE,"E15.45.4"),sQuery(id+"F0.wireOp",EDGE,"E15.45.6"),sQuery(id+"F0.wireOp",EDGE,"E15.45.7"),sQuery(id+"F0.wireOp",EDGE,"E15.45.8"),sQuery(id+"F0.wireOp",EDGE,"E15.45.9"),sQuery(id+"F0.wireOp",EDGE,"E15.46.2"),sQuery(id+"F0.wireOp",EDGE,"E15.46.4"),sQuery(id+"F0.wireOp",EDGE,"E15.46.6"),sQuery(id+"F0.wireOp",EDGE,"E15.46.7"),sQuery(id+"F0.wireOp",EDGE,"E15.46.8"),sQuery(id+"F0.wireOp",EDGE,"E15.46.9"),sQuery(id+"F0.wireOp",EDGE,"E15.47.2"),sQuery(id+"F0.wireOp",EDGE,"E15.47.4"),sQuery(id+"F0.wireOp",EDGE,"E15.47.6"),sQuery(id+"F0.wireOp",EDGE,"E15.47.7"),sQuery(id+"F0.wireOp",EDGE,"E15.47.8"),sQuery(id+"F0.wireOp",EDGE,"E15.47.9"),sQuery(id+"F0.wireOp",EDGE,"E15.48.2"),sQuery(id+"F0.wireOp",EDGE,"E15.48.4"),sQuery(id+"F0.wireOp",EDGE,"E15.48.6"),sQuery(id+"F0.wireOp",EDGE,"E15.48.7"),sQuery(id+"F0.wireOp",EDGE,"E15.48.8"),sQuery(id+"F0.wireOp",EDGE,"E15.48.9"),sQuery(id+"F0.wireOp",EDGE,"E15.49.2"),sQuery(id+"F0.wireOp",EDGE,"E15.49.4"),sQuery(id+"F0.wireOp",EDGE,"E15.49.6"),sQuery(id+"F0.wireOp",EDGE,"E15.49.7"),sQuery(id+"F0.wireOp",EDGE,"E15.49.8"),sQuery(id+"F0.wireOp",EDGE,"E15.49.9"),sQuery(id+"F0.wireOp",EDGE,"E16")])],"isStart":true});
            extrude(context, id + "F3", {"entities" : qUnion([Q0]), "operationType" : NewBodyOperationType.REMOVE, "endBound" : BoundingType.UP_TO_SURFACE, "oppositeDirection" : true, "endBoundEntityFace" : qUnion([Q1]), "depth" : 25 * mm});
        }
        {
            var Q0;
            Q0=makeQuery(id+"F1.opExtrude","CAP_FACE",FACE,{"disambiguationData":[OSD([sQuery(id+"F0.wireOp",EDGE,"E7"),sQuery(id+"F0.wireOp",EDGE,"E8"),sQuery(id+"F0.wireOp",EDGE,"E9"),sQuery(id+"F0.wireOp",EDGE,"E11"),sQuery(id+"F0.wireOp",EDGE,"E13"),sQuery(id+"F0.wireOp",EDGE,"E14"),sQuery(id+"F0.wireOp",EDGE,"E15.1.2"),sQuery(id+"F0.wireOp",EDGE,"E15.1.4"),sQuery(id+"F0.wireOp",EDGE,"E15.1.6"),sQuery(id+"F0.wireOp",EDGE,"E15.1.7"),sQuery(id+"F0.wireOp",EDGE,"E15.1.8"),sQuery(id+"F0.wireOp",EDGE,"E15.1.9"),sQuery(id+"F0.wireOp",EDGE,"E15.2.2"),sQuery(id+"F0.wireOp",EDGE,"E15.2.4"),sQuery(id+"F0.wireOp",EDGE,"E15.2.6"),sQuery(id+"F0.wireOp",EDGE,"E15.2.7"),sQuery(id+"F0.wireOp",EDGE,"E15.2.8"),sQuery(id+"F0.wireOp",EDGE,"E15.2.9"),sQuery(id+"F0.wireOp",EDGE,"E15.3.2"),sQuery(id+"F0.wireOp",EDGE,"E15.3.4"),sQuery(id+"F0.wireOp",EDGE,"E15.3.6"),sQuery(id+"F0.wireOp",EDGE,"E15.3.7"),sQuery(id+"F0.wireOp",EDGE,"E15.3.8"),sQuery(id+"F0.wireOp",EDGE,"E15.3.9"),sQuery(id+"F0.wireOp",EDGE,"E15.4.2"),sQuery(id+"F0.wireOp",EDGE,"E15.4.4"),sQuery(id+"F0.wireOp",EDGE,"E15.4.6"),sQuery(id+"F0.wireOp",EDGE,"E15.4.7"),sQuery(id+"F0.wireOp",EDGE,"E15.4.8"),sQuery(id+"F0.wireOp",EDGE,"E15.4.9"),sQuery(id+"F0.wireOp",EDGE,"E15.5.2"),sQuery(id+"F0.wireOp",EDGE,"E15.5.4"),sQuery(id+"F0.wireOp",EDGE,"E15.5.6"),sQuery(id+"F0.wireOp",EDGE,"E15.5.7"),sQuery(id+"F0.wireOp",EDGE,"E15.5.8"),sQuery(id+"F0.wireOp",EDGE,"E15.5.9"),sQuery(id+"F0.wireOp",EDGE,"E15.6.2"),sQuery(id+"F0.wireOp",EDGE,"E15.6.4"),sQuery(id+"F0.wireOp",EDGE,"E15.6.6"),sQuery(id+"F0.wireOp",EDGE,"E15.6.7"),sQuery(id+"F0.wireOp",EDGE,"E15.6.8"),sQuery(id+"F0.wireOp",EDGE,"E15.6.9"),sQuery(id+"F0.wireOp",EDGE,"E15.7.2"),sQuery(id+"F0.wireOp",EDGE,"E15.7.4"),sQuery(id+"F0.wireOp",EDGE,"E15.7.6"),sQuery(id+"F0.wireOp",EDGE,"E15.7.7"),sQuery(id+"F0.wireOp",EDGE,"E15.7.8"),sQuery(id+"F0.wireOp",EDGE,"E15.7.9"),sQuery(id+"F0.wireOp",EDGE,"E15.8.2"),sQuery(id+"F0.wireOp",EDGE,"E15.8.4"),sQuery(id+"F0.wireOp",EDGE,"E15.8.6"),sQuery(id+"F0.wireOp",EDGE,"E15.8.7"),sQuery(id+"F0.wireOp",EDGE,"E15.8.8"),sQuery(id+"F0.wireOp",EDGE,"E15.8.9"),sQuery(id+"F0.wireOp",EDGE,"E15.9.2"),sQuery(id+"F0.wireOp",EDGE,"E15.9.4"),sQuery(id+"F0.wireOp",EDGE,"E15.9.6"),sQuery(id+"F0.wireOp",EDGE,"E15.9.7"),sQuery(id+"F0.wireOp",EDGE,"E15.9.8"),sQuery(id+"F0.wireOp",EDGE,"E15.9.9"),sQuery(id+"F0.wireOp",EDGE,"E15.10.2"),sQuery(id+"F0.wireOp",EDGE,"E15.10.4"),sQuery(id+"F0.wireOp",EDGE,"E15.10.6"),sQuery(id+"F0.wireOp",EDGE,"E15.10.7"),sQuery(id+"F0.wireOp",EDGE,"E15.10.8"),sQuery(id+"F0.wireOp",EDGE,"E15.10.9"),sQuery(id+"F0.wireOp",EDGE,"E15.11.2"),sQuery(id+"F0.wireOp",EDGE,"E15.11.4"),sQuery(id+"F0.wireOp",EDGE,"E15.11.6"),sQuery(id+"F0.wireOp",EDGE,"E15.11.7"),sQuery(id+"F0.wireOp",EDGE,"E15.11.8"),sQuery(id+"F0.wireOp",EDGE,"E15.11.9"),sQuery(id+"F0.wireOp",EDGE,"E15.12.2"),sQuery(id+"F0.wireOp",EDGE,"E15.12.4"),sQuery(id+"F0.wireOp",EDGE,"E15.12.6"),sQuery(id+"F0.wireOp",EDGE,"E15.12.7"),sQuery(id+"F0.wireOp",EDGE,"E15.12.8"),sQuery(id+"F0.wireOp",EDGE,"E15.12.9"),sQuery(id+"F0.wireOp",EDGE,"E15.13.2"),sQuery(id+"F0.wireOp",EDGE,"E15.13.4"),sQuery(id+"F0.wireOp",EDGE,"E15.13.6"),sQuery(id+"F0.wireOp",EDGE,"E15.13.7"),sQuery(id+"F0.wireOp",EDGE,"E15.13.8"),sQuery(id+"F0.wireOp",EDGE,"E15.13.9"),sQuery(id+"F0.wireOp",EDGE,"E15.14.2"),sQuery(id+"F0.wireOp",EDGE,"E15.14.4"),sQuery(id+"F0.wireOp",EDGE,"E15.14.6"),sQuery(id+"F0.wireOp",EDGE,"E15.14.7"),sQuery(id+"F0.wireOp",EDGE,"E15.14.8"),sQuery(id+"F0.wireOp",EDGE,"E15.14.9"),sQuery(id+"F0.wireOp",EDGE,"E15.15.2"),sQuery(id+"F0.wireOp",EDGE,"E15.15.4"),sQuery(id+"F0.wireOp",EDGE,"E15.15.6"),sQuery(id+"F0.wireOp",EDGE,"E15.15.7"),sQuery(id+"F0.wireOp",EDGE,"E15.15.8"),sQuery(id+"F0.wireOp",EDGE,"E15.15.9"),sQuery(id+"F0.wireOp",EDGE,"E15.16.2"),sQuery(id+"F0.wireOp",EDGE,"E15.16.4"),sQuery(id+"F0.wireOp",EDGE,"E15.16.6"),sQuery(id+"F0.wireOp",EDGE,"E15.16.7"),sQuery(id+"F0.wireOp",EDGE,"E15.16.8"),sQuery(id+"F0.wireOp",EDGE,"E15.16.9"),sQuery(id+"F0.wireOp",EDGE,"E15.17.2"),sQuery(id+"F0.wireOp",EDGE,"E15.17.4"),sQuery(id+"F0.wireOp",EDGE,"E15.17.6"),sQuery(id+"F0.wireOp",EDGE,"E15.17.7"),sQuery(id+"F0.wireOp",EDGE,"E15.17.8"),sQuery(id+"F0.wireOp",EDGE,"E15.17.9"),sQuery(id+"F0.wireOp",EDGE,"E15.18.2"),sQuery(id+"F0.wireOp",EDGE,"E15.18.4"),sQuery(id+"F0.wireOp",EDGE,"E15.18.6"),sQuery(id+"F0.wireOp",EDGE,"E15.18.7"),sQuery(id+"F0.wireOp",EDGE,"E15.18.8"),sQuery(id+"F0.wireOp",EDGE,"E15.18.9"),sQuery(id+"F0.wireOp",EDGE,"E15.19.2"),sQuery(id+"F0.wireOp",EDGE,"E15.19.4"),sQuery(id+"F0.wireOp",EDGE,"E15.19.6"),sQuery(id+"F0.wireOp",EDGE,"E15.19.7"),sQuery(id+"F0.wireOp",EDGE,"E15.19.8"),sQuery(id+"F0.wireOp",EDGE,"E15.19.9"),sQuery(id+"F0.wireOp",EDGE,"E15.20.2"),sQuery(id+"F0.wireOp",EDGE,"E15.20.4"),sQuery(id+"F0.wireOp",EDGE,"E15.20.6"),sQuery(id+"F0.wireOp",EDGE,"E15.20.7"),sQuery(id+"F0.wireOp",EDGE,"E15.20.8"),sQuery(id+"F0.wireOp",EDGE,"E15.20.9"),sQuery(id+"F0.wireOp",EDGE,"E15.21.2"),sQuery(id+"F0.wireOp",EDGE,"E15.21.4"),sQuery(id+"F0.wireOp",EDGE,"E15.21.6"),sQuery(id+"F0.wireOp",EDGE,"E15.21.7"),sQuery(id+"F0.wireOp",EDGE,"E15.21.8"),sQuery(id+"F0.wireOp",EDGE,"E15.21.9"),sQuery(id+"F0.wireOp",EDGE,"E15.22.2"),sQuery(id+"F0.wireOp",EDGE,"E15.22.4"),sQuery(id+"F0.wireOp",EDGE,"E15.22.6"),sQuery(id+"F0.wireOp",EDGE,"E15.22.7"),sQuery(id+"F0.wireOp",EDGE,"E15.22.8"),sQuery(id+"F0.wireOp",EDGE,"E15.22.9"),sQuery(id+"F0.wireOp",EDGE,"E15.23.2"),sQuery(id+"F0.wireOp",EDGE,"E15.23.4"),sQuery(id+"F0.wireOp",EDGE,"E15.23.6"),sQuery(id+"F0.wireOp",EDGE,"E15.23.7"),sQuery(id+"F0.wireOp",EDGE,"E15.23.8"),sQuery(id+"F0.wireOp",EDGE,"E15.23.9"),sQuery(id+"F0.wireOp",EDGE,"E15.24.2"),sQuery(id+"F0.wireOp",EDGE,"E15.24.4"),sQuery(id+"F0.wireOp",EDGE,"E15.24.6"),sQuery(id+"F0.wireOp",EDGE,"E15.24.7"),sQuery(id+"F0.wireOp",EDGE,"E15.24.8"),sQuery(id+"F0.wireOp",EDGE,"E15.24.9"),sQuery(id+"F0.wireOp",EDGE,"E15.25.2"),sQuery(id+"F0.wireOp",EDGE,"E15.25.4"),sQuery(id+"F0.wireOp",EDGE,"E15.25.6"),sQuery(id+"F0.wireOp",EDGE,"E15.25.7"),sQuery(id+"F0.wireOp",EDGE,"E15.25.8"),sQuery(id+"F0.wireOp",EDGE,"E15.25.9"),sQuery(id+"F0.wireOp",EDGE,"E15.26.2"),sQuery(id+"F0.wireOp",EDGE,"E15.26.4"),sQuery(id+"F0.wireOp",EDGE,"E15.26.6"),sQuery(id+"F0.wireOp",EDGE,"E15.26.7"),sQuery(id+"F0.wireOp",EDGE,"E15.26.8"),sQuery(id+"F0.wireOp",EDGE,"E15.26.9"),sQuery(id+"F0.wireOp",EDGE,"E15.27.2"),sQuery(id+"F0.wireOp",EDGE,"E15.27.4"),sQuery(id+"F0.wireOp",EDGE,"E15.27.6"),sQuery(id+"F0.wireOp",EDGE,"E15.27.7"),sQuery(id+"F0.wireOp",EDGE,"E15.27.8"),sQuery(id+"F0.wireOp",EDGE,"E15.27.9"),sQuery(id+"F0.wireOp",EDGE,"E15.28.2"),sQuery(id+"F0.wireOp",EDGE,"E15.28.4"),sQuery(id+"F0.wireOp",EDGE,"E15.28.6"),sQuery(id+"F0.wireOp",EDGE,"E15.28.7"),sQuery(id+"F0.wireOp",EDGE,"E15.28.8"),sQuery(id+"F0.wireOp",EDGE,"E15.28.9"),sQuery(id+"F0.wireOp",EDGE,"E15.29.2"),sQuery(id+"F0.wireOp",EDGE,"E15.29.4"),sQuery(id+"F0.wireOp",EDGE,"E15.29.6"),sQuery(id+"F0.wireOp",EDGE,"E15.29.7"),sQuery(id+"F0.wireOp",EDGE,"E15.29.8"),sQuery(id+"F0.wireOp",EDGE,"E15.29.9"),sQuery(id+"F0.wireOp",EDGE,"E15.30.2"),sQuery(id+"F0.wireOp",EDGE,"E15.30.4"),sQuery(id+"F0.wireOp",EDGE,"E15.30.6"),sQuery(id+"F0.wireOp",EDGE,"E15.30.7"),sQuery(id+"F0.wireOp",EDGE,"E15.30.8"),sQuery(id+"F0.wireOp",EDGE,"E15.30.9"),sQuery(id+"F0.wireOp",EDGE,"E15.31.2"),sQuery(id+"F0.wireOp",EDGE,"E15.31.4"),sQuery(id+"F0.wireOp",EDGE,"E15.31.6"),sQuery(id+"F0.wireOp",EDGE,"E15.31.7"),sQuery(id+"F0.wireOp",EDGE,"E15.31.8"),sQuery(id+"F0.wireOp",EDGE,"E15.31.9"),sQuery(id+"F0.wireOp",EDGE,"E15.32.2"),sQuery(id+"F0.wireOp",EDGE,"E15.32.4"),sQuery(id+"F0.wireOp",EDGE,"E15.32.6"),sQuery(id+"F0.wireOp",EDGE,"E15.32.7"),sQuery(id+"F0.wireOp",EDGE,"E15.32.8"),sQuery(id+"F0.wireOp",EDGE,"E15.32.9"),sQuery(id+"F0.wireOp",EDGE,"E15.33.2"),sQuery(id+"F0.wireOp",EDGE,"E15.33.4"),sQuery(id+"F0.wireOp",EDGE,"E15.33.6"),sQuery(id+"F0.wireOp",EDGE,"E15.33.7"),sQuery(id+"F0.wireOp",EDGE,"E15.33.8"),sQuery(id+"F0.wireOp",EDGE,"E15.33.9"),sQuery(id+"F0.wireOp",EDGE,"E15.34.2"),sQuery(id+"F0.wireOp",EDGE,"E15.34.4"),sQuery(id+"F0.wireOp",EDGE,"E15.34.6"),sQuery(id+"F0.wireOp",EDGE,"E15.34.7"),sQuery(id+"F0.wireOp",EDGE,"E15.34.8"),sQuery(id+"F0.wireOp",EDGE,"E15.34.9"),sQuery(id+"F0.wireOp",EDGE,"E15.35.2"),sQuery(id+"F0.wireOp",EDGE,"E15.35.4"),sQuery(id+"F0.wireOp",EDGE,"E15.35.6"),sQuery(id+"F0.wireOp",EDGE,"E15.35.7"),sQuery(id+"F0.wireOp",EDGE,"E15.35.8"),sQuery(id+"F0.wireOp",EDGE,"E15.35.9"),sQuery(id+"F0.wireOp",EDGE,"E15.36.2"),sQuery(id+"F0.wireOp",EDGE,"E15.36.4"),sQuery(id+"F0.wireOp",EDGE,"E15.36.6"),sQuery(id+"F0.wireOp",EDGE,"E15.36.7"),sQuery(id+"F0.wireOp",EDGE,"E15.36.8"),sQuery(id+"F0.wireOp",EDGE,"E15.36.9"),sQuery(id+"F0.wireOp",EDGE,"E15.37.2"),sQuery(id+"F0.wireOp",EDGE,"E15.37.4"),sQuery(id+"F0.wireOp",EDGE,"E15.37.6"),sQuery(id+"F0.wireOp",EDGE,"E15.37.7"),sQuery(id+"F0.wireOp",EDGE,"E15.37.8"),sQuery(id+"F0.wireOp",EDGE,"E15.37.9"),sQuery(id+"F0.wireOp",EDGE,"E15.38.2"),sQuery(id+"F0.wireOp",EDGE,"E15.38.4"),sQuery(id+"F0.wireOp",EDGE,"E15.38.6"),sQuery(id+"F0.wireOp",EDGE,"E15.38.7"),sQuery(id+"F0.wireOp",EDGE,"E15.38.8"),sQuery(id+"F0.wireOp",EDGE,"E15.38.9"),sQuery(id+"F0.wireOp",EDGE,"E15.39.2"),sQuery(id+"F0.wireOp",EDGE,"E15.39.4"),sQuery(id+"F0.wireOp",EDGE,"E15.39.6"),sQuery(id+"F0.wireOp",EDGE,"E15.39.7"),sQuery(id+"F0.wireOp",EDGE,"E15.39.8"),sQuery(id+"F0.wireOp",EDGE,"E15.39.9"),sQuery(id+"F0.wireOp",EDGE,"E15.40.2"),sQuery(id+"F0.wireOp",EDGE,"E15.40.4"),sQuery(id+"F0.wireOp",EDGE,"E15.40.6"),sQuery(id+"F0.wireOp",EDGE,"E15.40.7"),sQuery(id+"F0.wireOp",EDGE,"E15.40.8"),sQuery(id+"F0.wireOp",EDGE,"E15.40.9"),sQuery(id+"F0.wireOp",EDGE,"E15.41.2"),sQuery(id+"F0.wireOp",EDGE,"E15.41.4"),sQuery(id+"F0.wireOp",EDGE,"E15.41.6"),sQuery(id+"F0.wireOp",EDGE,"E15.41.7"),sQuery(id+"F0.wireOp",EDGE,"E15.41.8"),sQuery(id+"F0.wireOp",EDGE,"E15.41.9"),sQuery(id+"F0.wireOp",EDGE,"E15.42.2"),sQuery(id+"F0.wireOp",EDGE,"E15.42.4"),sQuery(id+"F0.wireOp",EDGE,"E15.42.6"),sQuery(id+"F0.wireOp",EDGE,"E15.42.7"),sQuery(id+"F0.wireOp",EDGE,"E15.42.8"),sQuery(id+"F0.wireOp",EDGE,"E15.42.9"),sQuery(id+"F0.wireOp",EDGE,"E15.43.2"),sQuery(id+"F0.wireOp",EDGE,"E15.43.4"),sQuery(id+"F0.wireOp",EDGE,"E15.43.6"),sQuery(id+"F0.wireOp",EDGE,"E15.43.7"),sQuery(id+"F0.wireOp",EDGE,"E15.43.8"),sQuery(id+"F0.wireOp",EDGE,"E15.43.9"),sQuery(id+"F0.wireOp",EDGE,"E15.44.2"),sQuery(id+"F0.wireOp",EDGE,"E15.44.4"),sQuery(id+"F0.wireOp",EDGE,"E15.44.6"),sQuery(id+"F0.wireOp",EDGE,"E15.44.7"),sQuery(id+"F0.wireOp",EDGE,"E15.44.8"),sQuery(id+"F0.wireOp",EDGE,"E15.44.9"),sQuery(id+"F0.wireOp",EDGE,"E15.45.2"),sQuery(id+"F0.wireOp",EDGE,"E15.45.4"),sQuery(id+"F0.wireOp",EDGE,"E15.45.6"),sQuery(id+"F0.wireOp",EDGE,"E15.45.7"),sQuery(id+"F0.wireOp",EDGE,"E15.45.8"),sQuery(id+"F0.wireOp",EDGE,"E15.45.9"),sQuery(id+"F0.wireOp",EDGE,"E15.46.2"),sQuery(id+"F0.wireOp",EDGE,"E15.46.4"),sQuery(id+"F0.wireOp",EDGE,"E15.46.6"),sQuery(id+"F0.wireOp",EDGE,"E15.46.7"),sQuery(id+"F0.wireOp",EDGE,"E15.46.8"),sQuery(id+"F0.wireOp",EDGE,"E15.46.9"),sQuery(id+"F0.wireOp",EDGE,"E15.47.2"),sQuery(id+"F0.wireOp",EDGE,"E15.47.4"),sQuery(id+"F0.wireOp",EDGE,"E15.47.6"),sQuery(id+"F0.wireOp",EDGE,"E15.47.7"),sQuery(id+"F0.wireOp",EDGE,"E15.47.8"),sQuery(id+"F0.wireOp",EDGE,"E15.47.9"),sQuery(id+"F0.wireOp",EDGE,"E15.48.2"),sQuery(id+"F0.wireOp",EDGE,"E15.48.4"),sQuery(id+"F0.wireOp",EDGE,"E15.48.6"),sQuery(id+"F0.wireOp",EDGE,"E15.48.7"),sQuery(id+"F0.wireOp",EDGE,"E15.48.8"),sQuery(id+"F0.wireOp",EDGE,"E15.48.9"),sQuery(id+"F0.wireOp",EDGE,"E15.49.2"),sQuery(id+"F0.wireOp",EDGE,"E15.49.4"),sQuery(id+"F0.wireOp",EDGE,"E15.49.6"),sQuery(id+"F0.wireOp",EDGE,"E15.49.7"),sQuery(id+"F0.wireOp",EDGE,"E15.49.8"),sQuery(id+"F0.wireOp",EDGE,"E15.49.9"),sQuery(id+"F0.wireOp",EDGE,"E16")])],"isStart":false});
            var sketch = newSketch(context, id + "F4", { "sketchPlane" : qUnion([Q0])});
            skLineSegment(sketch, "E25", {"start": v(0, 0) * mm, "end": v(0, -31.2) * mm, "construction": true});
            skCircle(sketch, "E26", {"center": v(0, -8) * mm, "radius": 1 * mm});
            skCircle(sketch, "E27.1.0.0", {"center": v(0, -11.5) * mm, "radius": 1 * mm});
            skCircle(sketch, "E27.2.0.0", {"center": v(0, -15) * mm, "radius": 1 * mm});
            skCircle(sketch, "E27.3.0.0", {"center": v(0, -18.5) * mm, "radius": 1 * mm});
            skCircle(sketch, "E27.4.0.0", {"center": v(0, -22) * mm, "radius": 1 * mm});
            skCircle(sketch, "E27.5.0.0", {"center": v(0, -25.5) * mm, "radius": 1 * mm});
            skLineSegment(sketch, "E27.direction1", {"start": v(0, -8) * mm, "end": v(0, -11.5) * mm, "construction": true});
            skSolve(sketch);
        }
        {
            var Q0;
            Q0 = qSketchRegion(id + "F4", true);
            extrude(context, id + "F5", {"entities" : qUnion([Q0]), "operationType" : NewBodyOperationType.REMOVE, "oppositeDirection" : true, "depth" : 6 * mm});
        }
    });
